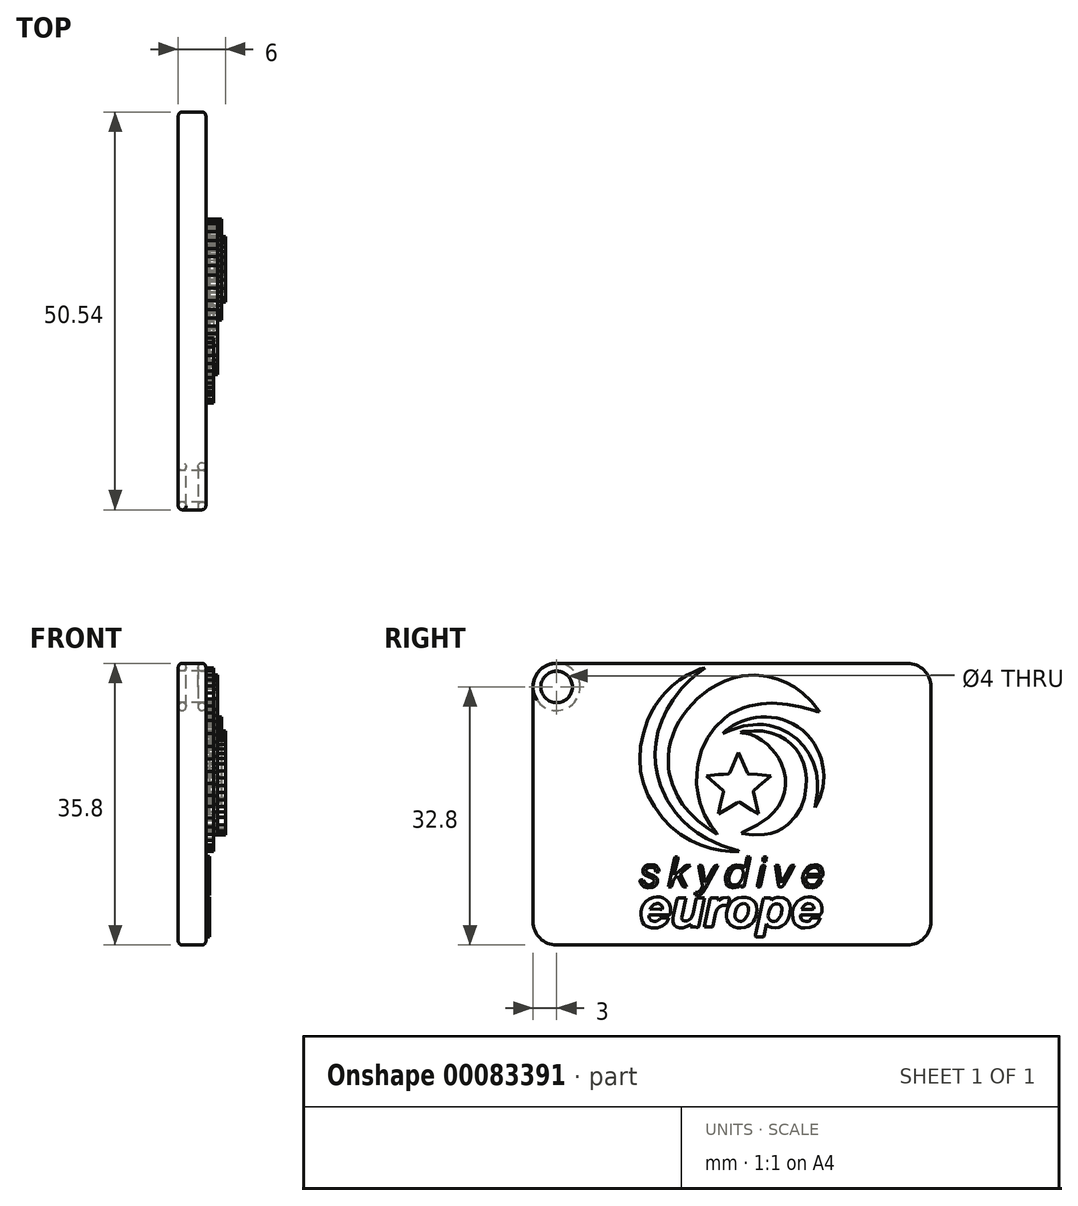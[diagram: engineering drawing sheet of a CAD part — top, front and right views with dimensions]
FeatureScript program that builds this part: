
annotation { "Feature Type Name" : "Feature", "Feature Type Description" : "" }
export const myFeature = defineFeature(function(context is Context, id is Id, definition is map)
    precondition{}
    {
        {
            var Q0;
            Q0=qCreatedBy(makeId("Right.planeOp"),FACE);
            var sketch = newSketch(context, id + "F0", { "sketchPlane" : qUnion([Q0])});
            skCircle(sketch, "E0", {"center": v(-22.27, 14.9) * mm, "radius": 2 * mm});
            skLineSegment(sketch, "E1", {"start": v(-25.27, 17.9) * mm, "end": v(-25.27, -17.9) * mm});
            skLineSegment(sketch, "E2", {"start": v(25.27, -17.9) * mm, "end": v(-25.27, -17.9) * mm});
            skLineSegment(sketch, "E3", {"start": v(25.27, 17.9) * mm, "end": v(-25.27, 17.9) * mm});
            skLineSegment(sketch, "E4", {"start": v(25.27, -17.9) * mm, "end": v(25.27, 17.9) * mm});
            skSolve(sketch);
        }
        {
            var Q0;
            Q0 = qSketchRegion(id + "F0", true);
            extrude(context, id + "F1", {"entities" : qUnion([Q0]), "depth" : 3.5 * mm});
        }
        {
            var Q0;
            Q0=makeQuery(id+"F1.opExtrude","SWEPT_EDGE",EDGE,{"disambiguationData":[OSD([sQuery(id+"F0.wireOp",EDGE,"E1"),sQuery(id+"F0.wireOp",EDGE,"E3")])]});
            var Q1;
            Q1=makeQuery(id+"F1.opExtrude","SWEPT_EDGE",EDGE,{"disambiguationData":[OSD([sQuery(id+"F0.wireOp",EDGE,"E1"),sQuery(id+"F0.wireOp",EDGE,"E2")])]});
            var Q2;
            Q2=makeQuery(id+"F1.opExtrude","SWEPT_EDGE",EDGE,{"disambiguationData":[OSD([sQuery(id+"F0.wireOp",EDGE,"E3"),sQuery(id+"F0.wireOp",EDGE,"E4")])]});
            var Q3;
            Q3=makeQuery(id+"F1.opExtrude","SWEPT_EDGE",EDGE,{"disambiguationData":[OSD([sQuery(id+"F0.wireOp",EDGE,"E2"),sQuery(id+"F0.wireOp",EDGE,"E4")])]});
            fillet(context, id + "F2", {"entities" : qUnion([Q0, Q1, Q2, Q3]), "radius" : 3 * mm, "tangentPropagation" : true, "allowEdgeOverflow" : false});
        }
        {
            var Q0;
            Q0=makeQuery(id+"F1.opExtrude","CAP_FACE",FACE,{"disambiguationData":[OSD([sQuery(id+"F0.wireOp",EDGE,"E0"),sQuery(id+"F0.wireOp",EDGE,"E1"),sQuery(id+"F0.wireOp",EDGE,"E2"),sQuery(id+"F0.wireOp",EDGE,"E3"),sQuery(id+"F0.wireOp",EDGE,"E4")])],"isStart":false});
            var Q1;
            Q1=makeQuery(id+"F1.opExtrude","CAP_FACE",FACE,{"disambiguationData":[OSD([sQuery(id+"F0.wireOp",EDGE,"E0"),sQuery(id+"F0.wireOp",EDGE,"E1"),sQuery(id+"F0.wireOp",EDGE,"E2"),sQuery(id+"F0.wireOp",EDGE,"E3"),sQuery(id+"F0.wireOp",EDGE,"E4")])],"isStart":true});
            fillet(context, id + "F3", {"entities" : qUnion([Q0, Q1]), "radius" : 0.5 * mm, "tangentPropagation" : true, "allowEdgeOverflow" : false});
        }
        {
            var Q0;
            Q0=makeQuery(id+"F1.opExtrude","CAP_EDGE",EDGE,{"disambiguationData":[OSD([sQuery(id+"F0.wireOp",EDGE,"E0")])],"isStart":false});
            var Q1;
            Q1=makeQuery(id+"F1.opExtrude","CAP_EDGE",EDGE,{"disambiguationData":[OSD([sQuery(id+"F0.wireOp",EDGE,"E0")])],"isStart":true});
            fillet(context, id + "F4", {"entities" : qUnion([Q0, Q1]), "radius" : 0.3 * mm, "tangentPropagation" : true, "allowEdgeOverflow" : false});
        }
        {
            var Q0;
            Q0=makeQuery(id+"F1.opExtrude","CAP_FACE",FACE,{"disambiguationData":[OSD([sQuery(id+"F0.wireOp",EDGE,"E0"),sQuery(id+"F0.wireOp",EDGE,"E1"),sQuery(id+"F0.wireOp",EDGE,"E2"),sQuery(id+"F0.wireOp",EDGE,"E3"),sQuery(id+"F0.wireOp",EDGE,"E4")])],"isStart":false});
            var sketch = newSketch(context, id + "F5", { "sketchPlane" : qUnion([Q0])});
            skLineSegment(sketch, "E5", {"start": v(4.97, 3.61) * mm, "end": v(3.46, 2.32) * mm});
            skLineSegment(sketch, "E6", {"start": v(3.46, 2.32) * mm, "end": v(3.2, 2.08) * mm});
            skLineSegment(sketch, "E7", {"start": v(3.2, 2.08) * mm, "end": v(2.92, 1.86) * mm});
            skLineSegment(sketch, "E8", {"start": v(2.92, 1.86) * mm, "end": v(2.8, 1.76) * mm});
            skLineSegment(sketch, "E9", {"start": v(2.8, 1.76) * mm, "end": v(2.75, 1.64) * mm});
            skLineSegment(sketch, "E10", {"start": v(2.75, 1.64) * mm, "end": v(2.74, 1.5) * mm});
            skLineSegment(sketch, "E11", {"start": v(2.74, 1.5) * mm, "end": v(2.78, 1.33) * mm});
            skLineSegment(sketch, "E12", {"start": v(2.78, 1.33) * mm, "end": v(3.38, -1.24) * mm});
            skLineSegment(sketch, "E13", {"start": v(3.38, -1.24) * mm, "end": v(2.49, -0.72) * mm});
            skLineSegment(sketch, "E14", {"start": v(2.49, -0.72) * mm, "end": v(1.01, 0.2) * mm});
            skLineSegment(sketch, "E15", {"start": v(1.01, 0.2) * mm, "end": v(0.83, 0.26) * mm});
            skLineSegment(sketch, "E16", {"start": v(0.83, 0.26) * mm, "end": v(0.62, 0.18) * mm});
            skLineSegment(sketch, "E17", {"start": v(0.62, 0.18) * mm, "end": v(-0.53, -0.53) * mm});
            skLineSegment(sketch, "E18", {"start": v(-0.53, -0.53) * mm, "end": v(-1.73, -1.25) * mm});
            skLineSegment(sketch, "E19", {"start": v(-1.73, -1.25) * mm, "end": v(-1.44, 0.02) * mm});
            skLineSegment(sketch, "E20", {"start": v(-1.44, 0.02) * mm, "end": v(-1.26, 0.8) * mm});
            skLineSegment(sketch, "E21", {"start": v(-1.26, 0.8) * mm, "end": v(-1.06, 1.56) * mm});
            skLineSegment(sketch, "E22", {"start": v(-1.06, 1.56) * mm, "end": v(-1.07, 1.68) * mm});
            skLineSegment(sketch, "E23", {"start": v(-1.07, 1.68) * mm, "end": v(-1.17, 1.77) * mm});
            skLineSegment(sketch, "E24", {"start": v(-1.17, 1.77) * mm, "end": v(-3.2, 3.53) * mm});
            skLineSegment(sketch, "E25", {"start": v(-3.2, 3.53) * mm, "end": v(-3.22, 3.56) * mm});
            skLineSegment(sketch, "E26", {"start": v(-3.22, 3.56) * mm, "end": v(-3.27, 3.61) * mm});
            skLineSegment(sketch, "E27", {"start": v(-3.27, 3.61) * mm, "end": v(-1.68, 3.76) * mm});
            skLineSegment(sketch, "E28", {"start": v(-1.68, 3.76) * mm, "end": v(-1.07, 3.8) * mm});
            skLineSegment(sketch, "E29", {"start": v(-1.07, 3.8) * mm, "end": v(-0.45, 3.86) * mm});
            skLineSegment(sketch, "E30", {"start": v(-0.45, 3.86) * mm, "end": v(-0.37, 3.89) * mm});
            skLineSegment(sketch, "E31", {"start": v(-0.37, 3.89) * mm, "end": v(-0.32, 3.94) * mm});
            skLineSegment(sketch, "E32", {"start": v(-0.32, 3.94) * mm, "end": v(-0.3, 4) * mm});
            skLineSegment(sketch, "E33", {"start": v(-0.3, 4) * mm, "end": v(-0.27, 4.05) * mm});
            skLineSegment(sketch, "E34", {"start": v(-0.27, 4.05) * mm, "end": v(0.8, 6.6) * mm});
            skLineSegment(sketch, "E35", {"start": v(0.8, 6.6) * mm, "end": v(1.1, 6.02) * mm});
            skLineSegment(sketch, "E36", {"start": v(1.1, 6.02) * mm, "end": v(1.34, 5.44) * mm});
            skLineSegment(sketch, "E37", {"start": v(1.34, 5.44) * mm, "end": v(1.94, 3.97) * mm});
            skLineSegment(sketch, "E38", {"start": v(1.94, 3.97) * mm, "end": v(2, 3.89) * mm});
            skLineSegment(sketch, "E39", {"start": v(2, 3.89) * mm, "end": v(2.08, 3.86) * mm});
            skLineSegment(sketch, "E40", {"start": v(2.08, 3.86) * mm, "end": v(3.22, 3.76) * mm});
            skLineSegment(sketch, "E41", {"start": v(3.22, 3.76) * mm, "end": v(4.97, 3.61) * mm});
            skLineSegment(sketch, "E42", {"start": v(4.37, -15.22) * mm, "end": v(4.05, -16.78) * mm});
            skLineSegment(sketch, "E43", {"start": v(4.05, -16.78) * mm, "end": v(4, -16.87) * mm});
            skLineSegment(sketch, "E44", {"start": v(4, -16.87) * mm, "end": v(3.9, -16.88) * mm});
            skLineSegment(sketch, "E45", {"start": v(3.9, -16.88) * mm, "end": v(3.46, -16.88) * mm});
            skLineSegment(sketch, "E46", {"start": v(3.46, -16.88) * mm, "end": v(3.28, -16.88) * mm});
            skLineSegment(sketch, "E47", {"start": v(3.28, -16.88) * mm, "end": v(3.14, -16.87) * mm});
            skLineSegment(sketch, "E48", {"start": v(3.14, -16.87) * mm, "end": v(3.05, -16.85) * mm});
            skLineSegment(sketch, "E49", {"start": v(3.05, -16.85) * mm, "end": v(3, -16.81) * mm});
            skLineSegment(sketch, "E50", {"start": v(3, -16.81) * mm, "end": v(2.98, -16.75) * mm});
            skLineSegment(sketch, "E51", {"start": v(2.98, -16.75) * mm, "end": v(2.98, -16.65) * mm});
            skLineSegment(sketch, "E52", {"start": v(2.98, -16.65) * mm, "end": v(3, -16.52) * mm});
            skLineSegment(sketch, "E53", {"start": v(3, -16.52) * mm, "end": v(3.05, -16.34) * mm});
            skLineSegment(sketch, "E54", {"start": v(3.05, -16.34) * mm, "end": v(3.75, -13.08) * mm});
            skLineSegment(sketch, "E55", {"start": v(3.75, -13.08) * mm, "end": v(3.94, -12.17) * mm});
            skLineSegment(sketch, "E56", {"start": v(3.94, -12.17) * mm, "end": v(3.98, -12.03) * mm});
            skLineSegment(sketch, "E57", {"start": v(3.98, -12.03) * mm, "end": v(4.04, -11.94) * mm});
            skLineSegment(sketch, "E58", {"start": v(4.04, -11.94) * mm, "end": v(4.15, -11.89) * mm});
            skLineSegment(sketch, "E59", {"start": v(4.15, -11.89) * mm, "end": v(4.3, -11.9) * mm});
            skLineSegment(sketch, "E60", {"start": v(4.3, -11.9) * mm, "end": v(4.5, -11.91) * mm});
            skLineSegment(sketch, "E61", {"start": v(4.5, -11.91) * mm, "end": v(4.72, -11.9) * mm});
            skLineSegment(sketch, "E62", {"start": v(4.72, -11.9) * mm, "end": v(4.86, -11.9) * mm});
            skLineSegment(sketch, "E63", {"start": v(4.86, -11.9) * mm, "end": v(4.96, -11.94) * mm});
            skLineSegment(sketch, "E64", {"start": v(4.96, -11.94) * mm, "end": v(5, -12.06) * mm});
            skLineSegment(sketch, "E65", {"start": v(5, -12.06) * mm, "end": v(4.99, -12.25) * mm});
            skLineSegment(sketch, "E66", {"start": v(4.99, -12.25) * mm, "end": v(5.22, -12.03) * mm});
            skLineSegment(sketch, "E67", {"start": v(5.22, -12.03) * mm, "end": v(5.47, -11.9) * mm});
            skLineSegment(sketch, "E68", {"start": v(5.47, -11.9) * mm, "end": v(5.73, -11.85) * mm});
            skLineSegment(sketch, "E69", {"start": v(5.73, -11.85) * mm, "end": v(6, -11.83) * mm});
            skLineSegment(sketch, "E70", {"start": v(6, -11.83) * mm, "end": v(6.52, -11.9) * mm});
            skLineSegment(sketch, "E71", {"start": v(6.52, -11.9) * mm, "end": v(6.98, -12.14) * mm});
            skLineSegment(sketch, "E72", {"start": v(6.98, -12.14) * mm, "end": v(7.13, -12.3) * mm});
            skLineSegment(sketch, "E73", {"start": v(7.13, -12.3) * mm, "end": v(7.24, -12.46) * mm});
            skLineSegment(sketch, "E74", {"start": v(7.24, -12.46) * mm, "end": v(7.32, -12.65) * mm});
            skLineSegment(sketch, "E75", {"start": v(7.32, -12.65) * mm, "end": v(7.37, -12.86) * mm});
            skLineSegment(sketch, "E76", {"start": v(7.37, -12.86) * mm, "end": v(7.41, -13.26) * mm});
            skLineSegment(sketch, "E77", {"start": v(7.41, -13.26) * mm, "end": v(7.4, -13.68) * mm});
            skLineSegment(sketch, "E78", {"start": v(7.4, -13.68) * mm, "end": v(7.31, -14.1) * mm});
            skLineSegment(sketch, "E79", {"start": v(7.31, -14.1) * mm, "end": v(7.18, -14.51) * mm});
            skLineSegment(sketch, "E80", {"start": v(7.18, -14.51) * mm, "end": v(6.98, -14.89) * mm});
            skLineSegment(sketch, "E81", {"start": v(6.98, -14.89) * mm, "end": v(6.71, -15.21) * mm});
            skLineSegment(sketch, "E82", {"start": v(6.71, -15.21) * mm, "end": v(6.38, -15.47) * mm});
            skLineSegment(sketch, "E83", {"start": v(6.38, -15.47) * mm, "end": v(5.98, -15.64) * mm});
            skLineSegment(sketch, "E84", {"start": v(5.98, -15.64) * mm, "end": v(5.5, -15.71) * mm});
            skLineSegment(sketch, "E85", {"start": v(5.5, -15.71) * mm, "end": v(5.05, -15.67) * mm});
            skLineSegment(sketch, "E86", {"start": v(5.05, -15.67) * mm, "end": v(4.66, -15.5) * mm});
            skLineSegment(sketch, "E87", {"start": v(4.66, -15.5) * mm, "end": v(4.37, -15.22) * mm});
            skLineSegment(sketch, "E88", {"start": v(-8, -14.42) * mm, "end": v(-8.34, -15.06) * mm});
            skLineSegment(sketch, "E89", {"start": v(-8.34, -15.06) * mm, "end": v(-8.85, -15.49) * mm});
            skLineSegment(sketch, "E90", {"start": v(-8.85, -15.49) * mm, "end": v(-9.49, -15.7) * mm});
            skLineSegment(sketch, "E91", {"start": v(-9.49, -15.7) * mm, "end": v(-10.23, -15.7) * mm});
            skLineSegment(sketch, "E92", {"start": v(-10.23, -15.7) * mm, "end": v(-10.6, -15.61) * mm});
            skLineSegment(sketch, "E93", {"start": v(-10.6, -15.61) * mm, "end": v(-10.93, -15.47) * mm});
            skLineSegment(sketch, "E94", {"start": v(-10.93, -15.47) * mm, "end": v(-11.19, -15.25) * mm});
            skLineSegment(sketch, "E95", {"start": v(-11.19, -15.25) * mm, "end": v(-11.37, -14.96) * mm});
            skLineSegment(sketch, "E96", {"start": v(-11.37, -14.96) * mm, "end": v(-11.5, -14.52) * mm});
            skLineSegment(sketch, "E97", {"start": v(-11.5, -14.52) * mm, "end": v(-11.56, -14.06) * mm});
            skLineSegment(sketch, "E98", {"start": v(-11.56, -14.06) * mm, "end": v(-11.54, -13.6) * mm});
            skLineSegment(sketch, "E99", {"start": v(-11.54, -13.6) * mm, "end": v(-11.42, -13.14) * mm});
            skLineSegment(sketch, "E100", {"start": v(-11.42, -13.14) * mm, "end": v(-11.2, -12.72) * mm});
            skLineSegment(sketch, "E101", {"start": v(-11.2, -12.72) * mm, "end": v(-10.9, -12.36) * mm});
            skLineSegment(sketch, "E102", {"start": v(-10.9, -12.36) * mm, "end": v(-10.5, -12.06) * mm});
            skLineSegment(sketch, "E103", {"start": v(-10.5, -12.06) * mm, "end": v(-9.99, -11.87) * mm});
            skLineSegment(sketch, "E104", {"start": v(-9.99, -11.87) * mm, "end": v(-9.58, -11.8) * mm});
            skLineSegment(sketch, "E105", {"start": v(-9.58, -11.8) * mm, "end": v(-9.16, -11.81) * mm});
            skLineSegment(sketch, "E106", {"start": v(-9.16, -11.81) * mm, "end": v(-8.75, -11.92) * mm});
            skLineSegment(sketch, "E107", {"start": v(-8.75, -11.92) * mm, "end": v(-8.36, -12.14) * mm});
            skLineSegment(sketch, "E108", {"start": v(-8.36, -12.14) * mm, "end": v(-7.99, -12.57) * mm});
            skLineSegment(sketch, "E109", {"start": v(-7.99, -12.57) * mm, "end": v(-7.83, -13.1) * mm});
            skLineSegment(sketch, "E110", {"start": v(-7.83, -13.1) * mm, "end": v(-7.82, -13.45) * mm});
            skLineSegment(sketch, "E111", {"start": v(-7.82, -13.45) * mm, "end": v(-7.82, -13.8) * mm});
            skLineSegment(sketch, "E112", {"start": v(-7.82, -13.8) * mm, "end": v(-7.83, -13.93) * mm});
            skLineSegment(sketch, "E113", {"start": v(-7.83, -13.93) * mm, "end": v(-7.88, -14.01) * mm});
            skLineSegment(sketch, "E114", {"start": v(-7.88, -14.01) * mm, "end": v(-7.97, -14.05) * mm});
            skLineSegment(sketch, "E115", {"start": v(-7.97, -14.05) * mm, "end": v(-8.1, -14.06) * mm});
            skLineSegment(sketch, "E116", {"start": v(-8.1, -14.06) * mm, "end": v(-10.23, -14.06) * mm});
            skLineSegment(sketch, "E117", {"start": v(-10.23, -14.06) * mm, "end": v(-10.42, -14.08) * mm});
            skLineSegment(sketch, "E118", {"start": v(-10.42, -14.08) * mm, "end": v(-10.52, -14.16) * mm});
            skLineSegment(sketch, "E119", {"start": v(-10.52, -14.16) * mm, "end": v(-10.54, -14.3) * mm});
            skLineSegment(sketch, "E120", {"start": v(-10.54, -14.3) * mm, "end": v(-10.48, -14.5) * mm});
            skLineSegment(sketch, "E121", {"start": v(-10.48, -14.5) * mm, "end": v(-10.26, -14.77) * mm});
            skLineSegment(sketch, "E122", {"start": v(-10.26, -14.77) * mm, "end": v(-9.93, -14.9) * mm});
            skLineSegment(sketch, "E123", {"start": v(-9.93, -14.9) * mm, "end": v(-9.57, -14.87) * mm});
            skLineSegment(sketch, "E124", {"start": v(-9.57, -14.87) * mm, "end": v(-9.23, -14.63) * mm});
            skLineSegment(sketch, "E125", {"start": v(-9.23, -14.63) * mm, "end": v(-9.13, -14.53) * mm});
            skLineSegment(sketch, "E126", {"start": v(-9.13, -14.53) * mm, "end": v(-9.02, -14.46) * mm});
            skLineSegment(sketch, "E127", {"start": v(-9.02, -14.46) * mm, "end": v(-8.9, -14.42) * mm});
            skLineSegment(sketch, "E128", {"start": v(-8.9, -14.42) * mm, "end": v(-8.77, -14.42) * mm});
            skLineSegment(sketch, "E129", {"start": v(-8.77, -14.42) * mm, "end": v(-8, -14.42) * mm});
            skLineSegment(sketch, "E130", {"start": v(11.25, -14.42) * mm, "end": v(10.9, -15.08) * mm});
            skLineSegment(sketch, "E131", {"start": v(10.9, -15.08) * mm, "end": v(10.45, -15.48) * mm});
            skLineSegment(sketch, "E132", {"start": v(10.45, -15.48) * mm, "end": v(9.92, -15.67) * mm});
            skLineSegment(sketch, "E133", {"start": v(9.92, -15.67) * mm, "end": v(9.3, -15.73) * mm});
            skLineSegment(sketch, "E134", {"start": v(9.3, -15.73) * mm, "end": v(8.84, -15.7) * mm});
            skLineSegment(sketch, "E135", {"start": v(8.84, -15.7) * mm, "end": v(8.42, -15.55) * mm});
            skLineSegment(sketch, "E136", {"start": v(8.42, -15.55) * mm, "end": v(8.07, -15.3) * mm});
            skLineSegment(sketch, "E137", {"start": v(8.07, -15.3) * mm, "end": v(7.84, -14.9) * mm});
            skLineSegment(sketch, "E138", {"start": v(7.84, -14.9) * mm, "end": v(7.72, -14.47) * mm});
            skLineSegment(sketch, "E139", {"start": v(7.72, -14.47) * mm, "end": v(7.68, -14.02) * mm});
            skLineSegment(sketch, "E140", {"start": v(7.68, -14.02) * mm, "end": v(7.71, -13.57) * mm});
            skLineSegment(sketch, "E141", {"start": v(7.71, -13.57) * mm, "end": v(7.83, -13.13) * mm});
            skLineSegment(sketch, "E142", {"start": v(7.83, -13.13) * mm, "end": v(8.03, -12.72) * mm});
            skLineSegment(sketch, "E143", {"start": v(8.03, -12.72) * mm, "end": v(8.33, -12.36) * mm});
            skLineSegment(sketch, "E144", {"start": v(8.33, -12.36) * mm, "end": v(8.73, -12.07) * mm});
            skLineSegment(sketch, "E145", {"start": v(8.73, -12.07) * mm, "end": v(9.23, -11.87) * mm});
            skLineSegment(sketch, "E146", {"start": v(9.23, -11.87) * mm, "end": v(9.66, -11.8) * mm});
            skLineSegment(sketch, "E147", {"start": v(9.66, -11.8) * mm, "end": v(10.1, -11.81) * mm});
            skLineSegment(sketch, "E148", {"start": v(10.1, -11.81) * mm, "end": v(10.52, -11.93) * mm});
            skLineSegment(sketch, "E149", {"start": v(10.52, -11.93) * mm, "end": v(10.92, -12.16) * mm});
            skLineSegment(sketch, "E150", {"start": v(10.92, -12.16) * mm, "end": v(11.12, -12.35) * mm});
            skLineSegment(sketch, "E151", {"start": v(11.12, -12.35) * mm, "end": v(11.27, -12.58) * mm});
            skLineSegment(sketch, "E152", {"start": v(11.27, -12.58) * mm, "end": v(11.37, -12.83) * mm});
            skLineSegment(sketch, "E153", {"start": v(11.37, -12.83) * mm, "end": v(11.42, -13.11) * mm});
            skLineSegment(sketch, "E154", {"start": v(11.42, -13.11) * mm, "end": v(11.43, -13.43) * mm});
            skLineSegment(sketch, "E155", {"start": v(11.43, -13.43) * mm, "end": v(11.42, -13.66) * mm});
            skLineSegment(sketch, "E156", {"start": v(11.42, -13.66) * mm, "end": v(11.4, -13.83) * mm});
            skLineSegment(sketch, "E157", {"start": v(11.4, -13.83) * mm, "end": v(11.33, -13.94) * mm});
            skLineSegment(sketch, "E158", {"start": v(11.33, -13.94) * mm, "end": v(11.22, -14) * mm});
            skLineSegment(sketch, "E159", {"start": v(11.22, -14) * mm, "end": v(11.05, -14.04) * mm});
            skLineSegment(sketch, "E160", {"start": v(11.05, -14.04) * mm, "end": v(10.82, -14.06) * mm});
            skLineSegment(sketch, "E161", {"start": v(10.82, -14.06) * mm, "end": v(10.5, -14.06) * mm});
            skLineSegment(sketch, "E162", {"start": v(10.5, -14.06) * mm, "end": v(8.92, -14.06) * mm});
            skLineSegment(sketch, "E163", {"start": v(8.92, -14.06) * mm, "end": v(8.82, -14.06) * mm});
            skLineSegment(sketch, "E164", {"start": v(8.82, -14.06) * mm, "end": v(8.76, -14.1) * mm});
            skLineSegment(sketch, "E165", {"start": v(8.76, -14.1) * mm, "end": v(8.73, -14.15) * mm});
            skLineSegment(sketch, "E166", {"start": v(8.73, -14.15) * mm, "end": v(8.72, -14.25) * mm});
            skLineSegment(sketch, "E167", {"start": v(8.72, -14.25) * mm, "end": v(8.75, -14.45) * mm});
            skLineSegment(sketch, "E168", {"start": v(8.75, -14.45) * mm, "end": v(8.82, -14.61) * mm});
            skLineSegment(sketch, "E169", {"start": v(8.82, -14.61) * mm, "end": v(8.95, -14.74) * mm});
            skLineSegment(sketch, "E170", {"start": v(8.95, -14.74) * mm, "end": v(9.12, -14.84) * mm});
            skLineSegment(sketch, "E171", {"start": v(9.12, -14.84) * mm, "end": v(9.38, -14.9) * mm});
            skLineSegment(sketch, "E172", {"start": v(9.38, -14.9) * mm, "end": v(9.63, -14.9) * mm});
            skLineSegment(sketch, "E173", {"start": v(9.63, -14.9) * mm, "end": v(9.85, -14.8) * mm});
            skLineSegment(sketch, "E174", {"start": v(9.85, -14.8) * mm, "end": v(10, -14.66) * mm});
            skLineSegment(sketch, "E175", {"start": v(10, -14.66) * mm, "end": v(10.1, -14.52) * mm});
            skLineSegment(sketch, "E176", {"start": v(10.1, -14.52) * mm, "end": v(10.22, -14.45) * mm});
            skLineSegment(sketch, "E177", {"start": v(10.22, -14.45) * mm, "end": v(10.36, -14.42) * mm});
            skLineSegment(sketch, "E178", {"start": v(10.36, -14.42) * mm, "end": v(10.5, -14.42) * mm});
            skLineSegment(sketch, "E179", {"start": v(10.5, -14.42) * mm, "end": v(11.25, -14.42) * mm});
            skLineSegment(sketch, "E180", {"start": v(3.15, -13.4) * mm, "end": v(3.14, -13.83) * mm});
            skLineSegment(sketch, "E181", {"start": v(3.14, -13.83) * mm, "end": v(3.06, -14.21) * mm});
            skLineSegment(sketch, "E182", {"start": v(3.06, -14.21) * mm, "end": v(2.93, -14.56) * mm});
            skLineSegment(sketch, "E183", {"start": v(2.93, -14.56) * mm, "end": v(2.75, -14.87) * mm});
            skLineSegment(sketch, "E184", {"start": v(2.75, -14.87) * mm, "end": v(2.52, -15.14) * mm});
            skLineSegment(sketch, "E185", {"start": v(2.52, -15.14) * mm, "end": v(2.26, -15.36) * mm});
            skLineSegment(sketch, "E186", {"start": v(2.26, -15.36) * mm, "end": v(1.97, -15.52) * mm});
            skLineSegment(sketch, "E187", {"start": v(1.97, -15.52) * mm, "end": v(1.65, -15.64) * mm});
            skLineSegment(sketch, "E188", {"start": v(1.65, -15.64) * mm, "end": v(1.16, -15.73) * mm});
            skLineSegment(sketch, "E189", {"start": v(1.16, -15.73) * mm, "end": v(0.69, -15.72) * mm});
            skLineSegment(sketch, "E190", {"start": v(0.69, -15.72) * mm, "end": v(0.23, -15.6) * mm});
            skLineSegment(sketch, "E191", {"start": v(0.23, -15.6) * mm, "end": v(-0.2, -15.34) * mm});
            skLineSegment(sketch, "E192", {"start": v(-0.2, -15.34) * mm, "end": v(-0.47, -15.04) * mm});
            skLineSegment(sketch, "E193", {"start": v(-0.47, -15.04) * mm, "end": v(-0.63, -14.7) * mm});
            skLineSegment(sketch, "E194", {"start": v(-0.63, -14.7) * mm, "end": v(-0.69, -14.3) * mm});
            skLineSegment(sketch, "E195", {"start": v(-0.69, -14.3) * mm, "end": v(-0.68, -13.9) * mm});
            skLineSegment(sketch, "E196", {"start": v(-0.68, -13.9) * mm, "end": v(-0.57, -13.3) * mm});
            skLineSegment(sketch, "E197", {"start": v(-0.57, -13.3) * mm, "end": v(-0.3, -12.74) * mm});
            skLineSegment(sketch, "E198", {"start": v(-0.3, -12.74) * mm, "end": v(0, -12.38) * mm});
            skLineSegment(sketch, "E199", {"start": v(0, -12.38) * mm, "end": v(0.35, -12.1) * mm});
            skLineSegment(sketch, "E200", {"start": v(0.35, -12.1) * mm, "end": v(0.75, -11.91) * mm});
            skLineSegment(sketch, "E201", {"start": v(0.75, -11.91) * mm, "end": v(1.22, -11.84) * mm});
            skLineSegment(sketch, "E202", {"start": v(1.22, -11.84) * mm, "end": v(1.75, -11.84) * mm});
            skLineSegment(sketch, "E203", {"start": v(1.75, -11.84) * mm, "end": v(2.27, -11.95) * mm});
            skLineSegment(sketch, "E204", {"start": v(2.27, -11.95) * mm, "end": v(2.7, -12.2) * mm});
            skLineSegment(sketch, "E205", {"start": v(2.7, -12.2) * mm, "end": v(2.98, -12.53) * mm});
            skLineSegment(sketch, "E206", {"start": v(2.98, -12.53) * mm, "end": v(3.13, -12.93) * mm});
            skLineSegment(sketch, "E207", {"start": v(3.13, -12.93) * mm, "end": v(3.15, -13.4) * mm});
            skLineSegment(sketch, "E208", {"start": v(-3.46, -11.9) * mm, "end": v(-4.05, -14.79) * mm});
            skLineSegment(sketch, "E209", {"start": v(-4.05, -14.79) * mm, "end": v(-4.18, -15.41) * mm});
            skLineSegment(sketch, "E210", {"start": v(-4.18, -15.41) * mm, "end": v(-4.21, -15.5) * mm});
            skLineSegment(sketch, "E211", {"start": v(-4.21, -15.5) * mm, "end": v(-4.26, -15.58) * mm});
            skLineSegment(sketch, "E212", {"start": v(-4.26, -15.58) * mm, "end": v(-4.34, -15.62) * mm});
            skLineSegment(sketch, "E213", {"start": v(-4.34, -15.62) * mm, "end": v(-4.46, -15.62) * mm});
            skLineSegment(sketch, "E214", {"start": v(-4.46, -15.62) * mm, "end": v(-4.7, -15.61) * mm});
            skLineSegment(sketch, "E215", {"start": v(-4.7, -15.61) * mm, "end": v(-4.97, -15.62) * mm});
            skLineSegment(sketch, "E216", {"start": v(-4.97, -15.62) * mm, "end": v(-5.07, -15.62) * mm});
            skLineSegment(sketch, "E217", {"start": v(-5.07, -15.62) * mm, "end": v(-5.15, -15.61) * mm});
            skLineSegment(sketch, "E218", {"start": v(-5.15, -15.61) * mm, "end": v(-5.2, -15.6) * mm});
            skLineSegment(sketch, "E219", {"start": v(-5.2, -15.6) * mm, "end": v(-5.24, -15.57) * mm});
            skLineSegment(sketch, "E220", {"start": v(-5.24, -15.57) * mm, "end": v(-5.25, -15.53) * mm});
            skLineSegment(sketch, "E221", {"start": v(-5.25, -15.53) * mm, "end": v(-5.24, -15.46) * mm});
            skLineSegment(sketch, "E222", {"start": v(-5.24, -15.46) * mm, "end": v(-5.22, -15.37) * mm});
            skLineSegment(sketch, "E223", {"start": v(-5.22, -15.37) * mm, "end": v(-5.18, -15.25) * mm});
            skLineSegment(sketch, "E224", {"start": v(-5.18, -15.25) * mm, "end": v(-5.69, -15.56) * mm});
            skLineSegment(sketch, "E225", {"start": v(-5.69, -15.56) * mm, "end": v(-6.23, -15.73) * mm});
            skLineSegment(sketch, "E226", {"start": v(-6.23, -15.73) * mm, "end": v(-6.65, -15.73) * mm});
            skLineSegment(sketch, "E227", {"start": v(-6.65, -15.73) * mm, "end": v(-7.05, -15.58) * mm});
            skLineSegment(sketch, "E228", {"start": v(-7.05, -15.58) * mm, "end": v(-7.34, -15.32) * mm});
            skLineSegment(sketch, "E229", {"start": v(-7.34, -15.32) * mm, "end": v(-7.46, -14.98) * mm});
            skLineSegment(sketch, "E230", {"start": v(-7.46, -14.98) * mm, "end": v(-7.46, -14.51) * mm});
            skLineSegment(sketch, "E231", {"start": v(-7.46, -14.51) * mm, "end": v(-7.4, -14.04) * mm});
            skLineSegment(sketch, "E232", {"start": v(-7.4, -14.04) * mm, "end": v(-6.98, -12.12) * mm});
            skLineSegment(sketch, "E233", {"start": v(-6.98, -12.12) * mm, "end": v(-6.96, -12.02) * mm});
            skLineSegment(sketch, "E234", {"start": v(-6.96, -12.02) * mm, "end": v(-6.92, -11.95) * mm});
            skLineSegment(sketch, "E235", {"start": v(-6.92, -11.95) * mm, "end": v(-6.85, -11.9) * mm});
            skLineSegment(sketch, "E236", {"start": v(-6.85, -11.9) * mm, "end": v(-6.74, -11.9) * mm});
            skLineSegment(sketch, "E237", {"start": v(-6.74, -11.9) * mm, "end": v(-6.3, -11.9) * mm});
            skLineSegment(sketch, "E238", {"start": v(-6.3, -11.9) * mm, "end": v(-5.85, -11.9) * mm});
            skLineSegment(sketch, "E239", {"start": v(-5.85, -11.9) * mm, "end": v(-6.38, -14.35) * mm});
            skLineSegment(sketch, "E240", {"start": v(-6.38, -14.35) * mm, "end": v(-6.4, -14.48) * mm});
            skLineSegment(sketch, "E241", {"start": v(-6.4, -14.48) * mm, "end": v(-6.37, -14.6) * mm});
            skLineSegment(sketch, "E242", {"start": v(-6.37, -14.6) * mm, "end": v(-6.31, -14.7) * mm});
            skLineSegment(sketch, "E243", {"start": v(-6.31, -14.7) * mm, "end": v(-6.2, -14.78) * mm});
            skLineSegment(sketch, "E244", {"start": v(-6.2, -14.78) * mm, "end": v(-6.01, -14.84) * mm});
            skLineSegment(sketch, "E245", {"start": v(-6.01, -14.84) * mm, "end": v(-5.82, -14.85) * mm});
            skLineSegment(sketch, "E246", {"start": v(-5.82, -14.85) * mm, "end": v(-5.64, -14.82) * mm});
            skLineSegment(sketch, "E247", {"start": v(-5.64, -14.82) * mm, "end": v(-5.45, -14.72) * mm});
            skLineSegment(sketch, "E248", {"start": v(-5.45, -14.72) * mm, "end": v(-5.23, -14.5) * mm});
            skLineSegment(sketch, "E249", {"start": v(-5.23, -14.5) * mm, "end": v(-5.07, -14.24) * mm});
            skLineSegment(sketch, "E250", {"start": v(-5.07, -14.24) * mm, "end": v(-4.96, -13.96) * mm});
            skLineSegment(sketch, "E251", {"start": v(-4.96, -13.96) * mm, "end": v(-4.89, -13.66) * mm});
            skLineSegment(sketch, "E252", {"start": v(-4.89, -13.66) * mm, "end": v(-4.58, -12.1) * mm});
            skLineSegment(sketch, "E253", {"start": v(-4.58, -12.1) * mm, "end": v(-4.56, -12.02) * mm});
            skLineSegment(sketch, "E254", {"start": v(-4.56, -12.02) * mm, "end": v(-4.53, -11.96) * mm});
            skLineSegment(sketch, "E255", {"start": v(-4.53, -11.96) * mm, "end": v(-4.48, -11.91) * mm});
            skLineSegment(sketch, "E256", {"start": v(-4.48, -11.91) * mm, "end": v(-4.38, -11.9) * mm});
            skLineSegment(sketch, "E257", {"start": v(-4.38, -11.9) * mm, "end": v(-3.46, -11.9) * mm});
            skLineSegment(sketch, "E258", {"start": v(-1.72, -11.9) * mm, "end": v(-1.73, -12) * mm});
            skLineSegment(sketch, "E259", {"start": v(-1.73, -12) * mm, "end": v(-1.76, -12.07) * mm});
            skLineSegment(sketch, "E260", {"start": v(-1.76, -12.07) * mm, "end": v(-1.77, -12.15) * mm});
            skLineSegment(sketch, "E261", {"start": v(-1.77, -12.15) * mm, "end": v(-1.74, -12.24) * mm});
            skLineSegment(sketch, "E262", {"start": v(-1.74, -12.24) * mm, "end": v(-1.18, -11.92) * mm});
            skLineSegment(sketch, "E263", {"start": v(-1.18, -11.92) * mm, "end": v(-0.52, -11.83) * mm});
            skLineSegment(sketch, "E264", {"start": v(-0.52, -11.83) * mm, "end": v(-0.42, -11.85) * mm});
            skLineSegment(sketch, "E265", {"start": v(-0.42, -11.85) * mm, "end": v(-0.35, -11.89) * mm});
            skLineSegment(sketch, "E266", {"start": v(-0.35, -11.89) * mm, "end": v(-0.33, -11.95) * mm});
            skLineSegment(sketch, "E267", {"start": v(-0.33, -11.95) * mm, "end": v(-0.33, -12.04) * mm});
            skLineSegment(sketch, "E268", {"start": v(-0.33, -12.04) * mm, "end": v(-0.46, -12.7) * mm});
            skLineSegment(sketch, "E269", {"start": v(-0.46, -12.7) * mm, "end": v(-0.48, -12.77) * mm});
            skLineSegment(sketch, "E270", {"start": v(-0.48, -12.77) * mm, "end": v(-0.53, -12.83) * mm});
            skLineSegment(sketch, "E271", {"start": v(-0.53, -12.83) * mm, "end": v(-0.6, -12.86) * mm});
            skLineSegment(sketch, "E272", {"start": v(-0.6, -12.86) * mm, "end": v(-0.69, -12.86) * mm});
            skLineSegment(sketch, "E273", {"start": v(-0.69, -12.86) * mm, "end": v(-1.2, -12.86) * mm});
            skLineSegment(sketch, "E274", {"start": v(-1.2, -12.86) * mm, "end": v(-1.6, -13.02) * mm});
            skLineSegment(sketch, "E275", {"start": v(-1.6, -13.02) * mm, "end": v(-1.88, -13.36) * mm});
            skLineSegment(sketch, "E276", {"start": v(-1.88, -13.36) * mm, "end": v(-2.07, -13.86) * mm});
            skLineSegment(sketch, "E277", {"start": v(-2.07, -13.86) * mm, "end": v(-2.42, -15.48) * mm});
            skLineSegment(sketch, "E278", {"start": v(-2.42, -15.48) * mm, "end": v(-2.44, -15.55) * mm});
            skLineSegment(sketch, "E279", {"start": v(-2.44, -15.55) * mm, "end": v(-2.47, -15.6) * mm});
            skLineSegment(sketch, "E280", {"start": v(-2.47, -15.6) * mm, "end": v(-2.52, -15.61) * mm});
            skLineSegment(sketch, "E281", {"start": v(-2.52, -15.61) * mm, "end": v(-2.58, -15.62) * mm});
            skLineSegment(sketch, "E282", {"start": v(-2.58, -15.62) * mm, "end": v(-3.36, -15.62) * mm});
            skLineSegment(sketch, "E283", {"start": v(-3.36, -15.62) * mm, "end": v(-3.45, -15.61) * mm});
            skLineSegment(sketch, "E284", {"start": v(-3.45, -15.61) * mm, "end": v(-3.49, -15.58) * mm});
            skLineSegment(sketch, "E285", {"start": v(-3.49, -15.58) * mm, "end": v(-3.5, -15.53) * mm});
            skLineSegment(sketch, "E286", {"start": v(-3.5, -15.53) * mm, "end": v(-3.48, -15.44) * mm});
            skLineSegment(sketch, "E287", {"start": v(-3.48, -15.44) * mm, "end": v(-2.8, -12.09) * mm});
            skLineSegment(sketch, "E288", {"start": v(-2.8, -12.09) * mm, "end": v(-2.77, -12) * mm});
            skLineSegment(sketch, "E289", {"start": v(-2.77, -12) * mm, "end": v(-2.73, -11.94) * mm});
            skLineSegment(sketch, "E290", {"start": v(-2.73, -11.94) * mm, "end": v(-2.67, -11.9) * mm});
            skLineSegment(sketch, "E291", {"start": v(-2.67, -11.9) * mm, "end": v(-2.58, -11.9) * mm});
            skLineSegment(sketch, "E292", {"start": v(-2.58, -11.9) * mm, "end": v(-1.72, -11.9) * mm});
            skLineSegment(sketch, "E293", {"start": v(1.13, -10.5) * mm, "end": v(1.12, -10.43) * mm});
            skLineSegment(sketch, "E294", {"start": v(1.12, -10.43) * mm, "end": v(1.15, -10.37) * mm});
            skLineSegment(sketch, "E295", {"start": v(1.15, -10.37) * mm, "end": v(1.18, -10.31) * mm});
            skLineSegment(sketch, "E296", {"start": v(1.18, -10.31) * mm, "end": v(1.15, -10.25) * mm});
            skLineSegment(sketch, "E297", {"start": v(1.15, -10.25) * mm, "end": v(0.87, -10.48) * mm});
            skLineSegment(sketch, "E298", {"start": v(0.87, -10.48) * mm, "end": v(0.52, -10.6) * mm});
            skLineSegment(sketch, "E299", {"start": v(0.52, -10.6) * mm, "end": v(0.14, -10.62) * mm});
            skLineSegment(sketch, "E300", {"start": v(0.14, -10.62) * mm, "end": v(-0.24, -10.53) * mm});
            skLineSegment(sketch, "E301", {"start": v(-0.24, -10.53) * mm, "end": v(-0.54, -10.31) * mm});
            skLineSegment(sketch, "E302", {"start": v(-0.54, -10.31) * mm, "end": v(-0.73, -9.98) * mm});
            skLineSegment(sketch, "E303", {"start": v(-0.73, -9.98) * mm, "end": v(-0.81, -9.6) * mm});
            skLineSegment(sketch, "E304", {"start": v(-0.81, -9.6) * mm, "end": v(-0.8, -9.25) * mm});
            skLineSegment(sketch, "E305", {"start": v(-0.8, -9.25) * mm, "end": v(-0.64, -8.68) * mm});
            skLineSegment(sketch, "E306", {"start": v(-0.64, -8.68) * mm, "end": v(-0.34, -8.17) * mm});
            skLineSegment(sketch, "E307", {"start": v(-0.34, -8.17) * mm, "end": v(0.08, -7.82) * mm});
            skLineSegment(sketch, "E308", {"start": v(0.08, -7.82) * mm, "end": v(0.58, -7.7) * mm});
            skLineSegment(sketch, "E309", {"start": v(0.58, -7.7) * mm, "end": v(1.12, -7.8) * mm});
            skLineSegment(sketch, "E310", {"start": v(1.12, -7.8) * mm, "end": v(1.62, -8.11) * mm});
            skLineSegment(sketch, "E311", {"start": v(1.62, -8.11) * mm, "end": v(1.88, -6.82) * mm});
            skLineSegment(sketch, "E312", {"start": v(1.88, -6.82) * mm, "end": v(1.93, -6.7) * mm});
            skLineSegment(sketch, "E313", {"start": v(1.93, -6.7) * mm, "end": v(2.02, -6.67) * mm});
            skLineSegment(sketch, "E314", {"start": v(2.02, -6.67) * mm, "end": v(2.11, -6.68) * mm});
            skLineSegment(sketch, "E315", {"start": v(2.11, -6.68) * mm, "end": v(2.2, -6.7) * mm});
            skLineSegment(sketch, "E316", {"start": v(2.2, -6.7) * mm, "end": v(2.28, -6.7) * mm});
            skLineSegment(sketch, "E317", {"start": v(2.28, -6.7) * mm, "end": v(2.32, -6.74) * mm});
            skLineSegment(sketch, "E318", {"start": v(2.32, -6.74) * mm, "end": v(2.32, -6.8) * mm});
            skLineSegment(sketch, "E319", {"start": v(2.32, -6.8) * mm, "end": v(2.3, -6.87) * mm});
            skLineSegment(sketch, "E320", {"start": v(2.3, -6.87) * mm, "end": v(1.59, -10.24) * mm});
            skLineSegment(sketch, "E321", {"start": v(1.59, -10.24) * mm, "end": v(1.53, -10.42) * mm});
            skLineSegment(sketch, "E322", {"start": v(1.53, -10.42) * mm, "end": v(1.43, -10.5) * mm});
            skLineSegment(sketch, "E323", {"start": v(1.43, -10.5) * mm, "end": v(1.3, -10.53) * mm});
            skLineSegment(sketch, "E324", {"start": v(1.3, -10.53) * mm, "end": v(1.13, -10.5) * mm});
            skLineSegment(sketch, "E325", {"start": v(11.4, -9.63) * mm, "end": v(11.14, -10.18) * mm});
            skLineSegment(sketch, "E326", {"start": v(11.14, -10.18) * mm, "end": v(10.74, -10.5) * mm});
            skLineSegment(sketch, "E327", {"start": v(10.74, -10.5) * mm, "end": v(10.22, -10.63) * mm});
            skLineSegment(sketch, "E328", {"start": v(10.22, -10.63) * mm, "end": v(9.65, -10.57) * mm});
            skLineSegment(sketch, "E329", {"start": v(9.65, -10.57) * mm, "end": v(9.35, -10.4) * mm});
            skLineSegment(sketch, "E330", {"start": v(9.35, -10.4) * mm, "end": v(9.13, -10.13) * mm});
            skLineSegment(sketch, "E331", {"start": v(9.13, -10.13) * mm, "end": v(9, -9.78) * mm});
            skLineSegment(sketch, "E332", {"start": v(9, -9.78) * mm, "end": v(8.97, -9.37) * mm});
            skLineSegment(sketch, "E333", {"start": v(8.97, -9.37) * mm, "end": v(9.13, -8.64) * mm});
            skLineSegment(sketch, "E334", {"start": v(9.13, -8.64) * mm, "end": v(9.56, -8.02) * mm});
            skLineSegment(sketch, "E335", {"start": v(9.56, -8.02) * mm, "end": v(9.93, -7.8) * mm});
            skLineSegment(sketch, "E336", {"start": v(9.93, -7.8) * mm, "end": v(10.4, -7.7) * mm});
            skLineSegment(sketch, "E337", {"start": v(10.4, -7.7) * mm, "end": v(10.85, -7.73) * mm});
            skLineSegment(sketch, "E338", {"start": v(10.85, -7.73) * mm, "end": v(11.21, -7.9) * mm});
            skLineSegment(sketch, "E339", {"start": v(11.21, -7.9) * mm, "end": v(11.36, -8.06) * mm});
            skLineSegment(sketch, "E340", {"start": v(11.36, -8.06) * mm, "end": v(11.46, -8.25) * mm});
            skLineSegment(sketch, "E341", {"start": v(11.46, -8.25) * mm, "end": v(11.52, -8.46) * mm});
            skLineSegment(sketch, "E342", {"start": v(11.52, -8.46) * mm, "end": v(11.54, -8.68) * mm});
            skLineSegment(sketch, "E343", {"start": v(11.54, -8.68) * mm, "end": v(11.54, -8.87) * mm});
            skLineSegment(sketch, "E344", {"start": v(11.54, -8.87) * mm, "end": v(11.53, -9.02) * mm});
            skLineSegment(sketch, "E345", {"start": v(11.53, -9.02) * mm, "end": v(11.51, -9.12) * mm});
            skLineSegment(sketch, "E346", {"start": v(11.51, -9.12) * mm, "end": v(11.47, -9.19) * mm});
            skLineSegment(sketch, "E347", {"start": v(11.47, -9.19) * mm, "end": v(11.4, -9.23) * mm});
            skLineSegment(sketch, "E348", {"start": v(11.4, -9.23) * mm, "end": v(11.3, -9.25) * mm});
            skLineSegment(sketch, "E349", {"start": v(11.3, -9.25) * mm, "end": v(11.15, -9.26) * mm});
            skLineSegment(sketch, "E350", {"start": v(11.15, -9.26) * mm, "end": v(10.96, -9.26) * mm});
            skLineSegment(sketch, "E351", {"start": v(10.96, -9.26) * mm, "end": v(9.58, -9.26) * mm});
            skLineSegment(sketch, "E352", {"start": v(9.58, -9.26) * mm, "end": v(9.49, -9.27) * mm});
            skLineSegment(sketch, "E353", {"start": v(9.49, -9.27) * mm, "end": v(9.42, -9.3) * mm});
            skLineSegment(sketch, "E354", {"start": v(9.42, -9.3) * mm, "end": v(9.39, -9.35) * mm});
            skLineSegment(sketch, "E355", {"start": v(9.39, -9.35) * mm, "end": v(9.38, -9.45) * mm});
            skLineSegment(sketch, "E356", {"start": v(9.38, -9.45) * mm, "end": v(9.42, -9.72) * mm});
            skLineSegment(sketch, "E357", {"start": v(9.42, -9.72) * mm, "end": v(9.53, -9.96) * mm});
            skLineSegment(sketch, "E358", {"start": v(9.53, -9.96) * mm, "end": v(9.7, -10.14) * mm});
            skLineSegment(sketch, "E359", {"start": v(9.7, -10.14) * mm, "end": v(9.93, -10.26) * mm});
            skLineSegment(sketch, "E360", {"start": v(9.93, -10.26) * mm, "end": v(10.19, -10.28) * mm});
            skLineSegment(sketch, "E361", {"start": v(10.19, -10.28) * mm, "end": v(10.47, -10.23) * mm});
            skLineSegment(sketch, "E362", {"start": v(10.47, -10.23) * mm, "end": v(10.7, -10.09) * mm});
            skLineSegment(sketch, "E363", {"start": v(10.7, -10.09) * mm, "end": v(10.86, -9.88) * mm});
            skLineSegment(sketch, "E364", {"start": v(10.86, -9.88) * mm, "end": v(10.96, -9.72) * mm});
            skLineSegment(sketch, "E365", {"start": v(10.96, -9.72) * mm, "end": v(11.09, -9.64) * mm});
            skLineSegment(sketch, "E366", {"start": v(11.09, -9.64) * mm, "end": v(11.24, -9.62) * mm});
            skLineSegment(sketch, "E367", {"start": v(11.24, -9.62) * mm, "end": v(11.4, -9.63) * mm});
            skLineSegment(sketch, "E368", {"start": v(-5.29, -7.8) * mm, "end": v(-6.27, -8.6) * mm});
            skLineSegment(sketch, "E369", {"start": v(-6.27, -8.6) * mm, "end": v(-6.4, -8.71) * mm});
            skLineSegment(sketch, "E370", {"start": v(-6.4, -8.71) * mm, "end": v(-6.49, -8.83) * mm});
            skLineSegment(sketch, "E371", {"start": v(-6.49, -8.83) * mm, "end": v(-6.5, -8.97) * mm});
            skLineSegment(sketch, "E372", {"start": v(-6.5, -8.97) * mm, "end": v(-6.42, -9.16) * mm});
            skLineSegment(sketch, "E373", {"start": v(-6.42, -9.16) * mm, "end": v(-6.09, -9.81) * mm});
            skLineSegment(sketch, "E374", {"start": v(-6.09, -9.81) * mm, "end": v(-5.78, -10.5) * mm});
            skLineSegment(sketch, "E375", {"start": v(-5.78, -10.5) * mm, "end": v(-5.97, -10.53) * mm});
            skLineSegment(sketch, "E376", {"start": v(-5.97, -10.53) * mm, "end": v(-6.13, -10.5) * mm});
            skLineSegment(sketch, "E377", {"start": v(-6.13, -10.5) * mm, "end": v(-6.26, -10.4) * mm});
            skLineSegment(sketch, "E378", {"start": v(-6.26, -10.4) * mm, "end": v(-6.36, -10.23) * mm});
            skLineSegment(sketch, "E379", {"start": v(-6.36, -10.23) * mm, "end": v(-6.9, -9.13) * mm});
            skLineSegment(sketch, "E380", {"start": v(-6.9, -9.13) * mm, "end": v(-7.17, -9.3) * mm});
            skLineSegment(sketch, "E381", {"start": v(-7.17, -9.3) * mm, "end": v(-7.37, -9.54) * mm});
            skLineSegment(sketch, "E382", {"start": v(-7.37, -9.54) * mm, "end": v(-7.5, -9.82) * mm});
            skLineSegment(sketch, "E383", {"start": v(-7.5, -9.82) * mm, "end": v(-7.59, -10.15) * mm});
            skLineSegment(sketch, "E384", {"start": v(-7.59, -10.15) * mm, "end": v(-7.6, -10.28) * mm});
            skLineSegment(sketch, "E385", {"start": v(-7.6, -10.28) * mm, "end": v(-7.63, -10.37) * mm});
            skLineSegment(sketch, "E386", {"start": v(-7.63, -10.37) * mm, "end": v(-7.66, -10.44) * mm});
            skLineSegment(sketch, "E387", {"start": v(-7.66, -10.44) * mm, "end": v(-7.7, -10.48) * mm});
            skLineSegment(sketch, "E388", {"start": v(-7.7, -10.48) * mm, "end": v(-7.75, -10.5) * mm});
            skLineSegment(sketch, "E389", {"start": v(-7.75, -10.5) * mm, "end": v(-7.82, -10.52) * mm});
            skLineSegment(sketch, "E390", {"start": v(-7.82, -10.52) * mm, "end": v(-7.92, -10.51) * mm});
            skLineSegment(sketch, "E391", {"start": v(-7.92, -10.51) * mm, "end": v(-8.04, -10.5) * mm});
            skLineSegment(sketch, "E392", {"start": v(-8.04, -10.5) * mm, "end": v(-7.28, -6.91) * mm});
            skLineSegment(sketch, "E393", {"start": v(-7.28, -6.91) * mm, "end": v(-7.27, -6.84) * mm});
            skLineSegment(sketch, "E394", {"start": v(-7.27, -6.84) * mm, "end": v(-7.25, -6.78) * mm});
            skLineSegment(sketch, "E395", {"start": v(-7.25, -6.78) * mm, "end": v(-7.21, -6.72) * mm});
            skLineSegment(sketch, "E396", {"start": v(-7.21, -6.72) * mm, "end": v(-7.15, -6.69) * mm});
            skLineSegment(sketch, "E397", {"start": v(-7.15, -6.69) * mm, "end": v(-7, -6.67) * mm});
            skLineSegment(sketch, "E398", {"start": v(-7, -6.67) * mm, "end": v(-6.91, -6.71) * mm});
            skLineSegment(sketch, "E399", {"start": v(-6.91, -6.71) * mm, "end": v(-6.86, -6.8) * mm});
            skLineSegment(sketch, "E400", {"start": v(-6.86, -6.8) * mm, "end": v(-6.87, -6.94) * mm});
            skLineSegment(sketch, "E401", {"start": v(-6.87, -6.94) * mm, "end": v(-7.28, -8.72) * mm});
            skLineSegment(sketch, "E402", {"start": v(-7.28, -8.72) * mm, "end": v(-7.29, -8.82) * mm});
            skLineSegment(sketch, "E403", {"start": v(-7.29, -8.82) * mm, "end": v(-7.28, -8.96) * mm});
            skLineSegment(sketch, "E404", {"start": v(-7.28, -8.96) * mm, "end": v(-6.72, -8.53) * mm});
            skLineSegment(sketch, "E405", {"start": v(-6.72, -8.53) * mm, "end": v(-6.2, -8.07) * mm});
            skLineSegment(sketch, "E406", {"start": v(-6.2, -8.07) * mm, "end": v(-6, -7.92) * mm});
            skLineSegment(sketch, "E407", {"start": v(-6, -7.92) * mm, "end": v(-5.8, -7.8) * mm});
            skLineSegment(sketch, "E408", {"start": v(-5.8, -7.8) * mm, "end": v(-5.56, -7.76) * mm});
            skLineSegment(sketch, "E409", {"start": v(-5.56, -7.76) * mm, "end": v(-5.29, -7.8) * mm});
            skLineSegment(sketch, "E410", {"start": v(-10.25, -7.7) * mm, "end": v(-9.84, -7.73) * mm});
            skLineSegment(sketch, "E411", {"start": v(-9.84, -7.73) * mm, "end": v(-9.56, -7.85) * mm});
            skLineSegment(sketch, "E412", {"start": v(-9.56, -7.85) * mm, "end": v(-9.39, -8.07) * mm});
            skLineSegment(sketch, "E413", {"start": v(-9.39, -8.07) * mm, "end": v(-9.28, -8.34) * mm});
            skLineSegment(sketch, "E414", {"start": v(-9.28, -8.34) * mm, "end": v(-9.26, -8.41) * mm});
            skLineSegment(sketch, "E415", {"start": v(-9.26, -8.41) * mm, "end": v(-9.24, -8.5) * mm});
            skLineSegment(sketch, "E416", {"start": v(-9.24, -8.5) * mm, "end": v(-9.27, -8.57) * mm});
            skLineSegment(sketch, "E417", {"start": v(-9.27, -8.57) * mm, "end": v(-9.38, -8.6) * mm});
            skLineSegment(sketch, "E418", {"start": v(-9.38, -8.6) * mm, "end": v(-9.47, -8.61) * mm});
            skLineSegment(sketch, "E419", {"start": v(-9.47, -8.61) * mm, "end": v(-9.58, -8.62) * mm});
            skLineSegment(sketch, "E420", {"start": v(-9.58, -8.62) * mm, "end": v(-9.66, -8.58) * mm});
            skLineSegment(sketch, "E421", {"start": v(-9.66, -8.58) * mm, "end": v(-9.69, -8.43) * mm});
            skLineSegment(sketch, "E422", {"start": v(-9.69, -8.43) * mm, "end": v(-9.74, -8.27) * mm});
            skLineSegment(sketch, "E423", {"start": v(-9.74, -8.27) * mm, "end": v(-9.86, -8.14) * mm});
            skLineSegment(sketch, "E424", {"start": v(-9.86, -8.14) * mm, "end": v(-10.04, -8.05) * mm});
            skLineSegment(sketch, "E425", {"start": v(-10.04, -8.05) * mm, "end": v(-10.24, -8) * mm});
            skLineSegment(sketch, "E426", {"start": v(-10.24, -8) * mm, "end": v(-10.46, -8.02) * mm});
            skLineSegment(sketch, "E427", {"start": v(-10.46, -8.02) * mm, "end": v(-10.67, -8.1) * mm});
            skLineSegment(sketch, "E428", {"start": v(-10.67, -8.1) * mm, "end": v(-10.83, -8.22) * mm});
            skLineSegment(sketch, "E429", {"start": v(-10.83, -8.22) * mm, "end": v(-10.9, -8.37) * mm});
            skLineSegment(sketch, "E430", {"start": v(-10.9, -8.37) * mm, "end": v(-10.9, -8.51) * mm});
            skLineSegment(sketch, "E431", {"start": v(-10.9, -8.51) * mm, "end": v(-10.85, -8.62) * mm});
            skLineSegment(sketch, "E432", {"start": v(-10.85, -8.62) * mm, "end": v(-10.75, -8.71) * mm});
            skLineSegment(sketch, "E433", {"start": v(-10.75, -8.71) * mm, "end": v(-10.63, -8.78) * mm});
            skLineSegment(sketch, "E434", {"start": v(-10.63, -8.78) * mm, "end": v(-9.92, -9.11) * mm});
            skLineSegment(sketch, "E435", {"start": v(-9.92, -9.11) * mm, "end": v(-9.69, -9.26) * mm});
            skLineSegment(sketch, "E436", {"start": v(-9.69, -9.26) * mm, "end": v(-9.53, -9.43) * mm});
            skLineSegment(sketch, "E437", {"start": v(-9.53, -9.43) * mm, "end": v(-9.45, -9.63) * mm});
            skLineSegment(sketch, "E438", {"start": v(-9.45, -9.63) * mm, "end": v(-9.44, -9.86) * mm});
            skLineSegment(sketch, "E439", {"start": v(-9.44, -9.86) * mm, "end": v(-9.51, -10.08) * mm});
            skLineSegment(sketch, "E440", {"start": v(-9.51, -10.08) * mm, "end": v(-9.66, -10.3) * mm});
            skLineSegment(sketch, "E441", {"start": v(-9.66, -10.3) * mm, "end": v(-9.87, -10.47) * mm});
            skLineSegment(sketch, "E442", {"start": v(-9.87, -10.47) * mm, "end": v(-10.1, -10.57) * mm});
            skLineSegment(sketch, "E443", {"start": v(-10.1, -10.57) * mm, "end": v(-10.65, -10.63) * mm});
            skLineSegment(sketch, "E444", {"start": v(-10.65, -10.63) * mm, "end": v(-11.2, -10.48) * mm});
            skLineSegment(sketch, "E445", {"start": v(-11.2, -10.48) * mm, "end": v(-11.39, -10.35) * mm});
            skLineSegment(sketch, "E446", {"start": v(-11.39, -10.35) * mm, "end": v(-11.52, -10.17) * mm});
            skLineSegment(sketch, "E447", {"start": v(-11.52, -10.17) * mm, "end": v(-11.6, -9.97) * mm});
            skLineSegment(sketch, "E448", {"start": v(-11.6, -9.97) * mm, "end": v(-11.66, -9.76) * mm});
            skLineSegment(sketch, "E449", {"start": v(-11.66, -9.76) * mm, "end": v(-11.66, -9.7) * mm});
            skLineSegment(sketch, "E450", {"start": v(-11.66, -9.7) * mm, "end": v(-11.64, -9.64) * mm});
            skLineSegment(sketch, "E451", {"start": v(-11.64, -9.64) * mm, "end": v(-11.6, -9.62) * mm});
            skLineSegment(sketch, "E452", {"start": v(-11.6, -9.62) * mm, "end": v(-11.53, -9.63) * mm});
            skLineSegment(sketch, "E453", {"start": v(-11.53, -9.63) * mm, "end": v(-11.45, -9.63) * mm});
            skLineSegment(sketch, "E454", {"start": v(-11.45, -9.63) * mm, "end": v(-11.37, -9.61) * mm});
            skLineSegment(sketch, "E455", {"start": v(-11.37, -9.61) * mm, "end": v(-11.29, -9.64) * mm});
            skLineSegment(sketch, "E456", {"start": v(-11.29, -9.64) * mm, "end": v(-11.23, -9.75) * mm});
            skLineSegment(sketch, "E457", {"start": v(-11.23, -9.75) * mm, "end": v(-11.04, -10.08) * mm});
            skLineSegment(sketch, "E458", {"start": v(-11.04, -10.08) * mm, "end": v(-10.72, -10.27) * mm});
            skLineSegment(sketch, "E459", {"start": v(-10.72, -10.27) * mm, "end": v(-10.35, -10.28) * mm});
            skLineSegment(sketch, "E460", {"start": v(-10.35, -10.28) * mm, "end": v(-10, -10.1) * mm});
            skLineSegment(sketch, "E461", {"start": v(-10, -10.1) * mm, "end": v(-9.88, -9.92) * mm});
            skLineSegment(sketch, "E462", {"start": v(-9.88, -9.92) * mm, "end": v(-9.86, -9.75) * mm});
            skLineSegment(sketch, "E463", {"start": v(-9.86, -9.75) * mm, "end": v(-9.93, -9.58) * mm});
            skLineSegment(sketch, "E464", {"start": v(-9.93, -9.58) * mm, "end": v(-10.1, -9.45) * mm});
            skLineSegment(sketch, "E465", {"start": v(-10.1, -9.45) * mm, "end": v(-10.64, -9.2) * mm});
            skLineSegment(sketch, "E466", {"start": v(-10.64, -9.2) * mm, "end": v(-11, -9.04) * mm});
            skLineSegment(sketch, "E467", {"start": v(-11, -9.04) * mm, "end": v(-11.21, -8.83) * mm});
            skLineSegment(sketch, "E468", {"start": v(-11.21, -8.83) * mm, "end": v(-11.31, -8.57) * mm});
            skLineSegment(sketch, "E469", {"start": v(-11.31, -8.57) * mm, "end": v(-11.3, -8.26) * mm});
            skLineSegment(sketch, "E470", {"start": v(-11.3, -8.26) * mm, "end": v(-11.2, -8.04) * mm});
            skLineSegment(sketch, "E471", {"start": v(-11.2, -8.04) * mm, "end": v(-10.99, -7.86) * mm});
            skLineSegment(sketch, "E472", {"start": v(-10.99, -7.86) * mm, "end": v(-10.7, -7.75) * mm});
            skLineSegment(sketch, "E473", {"start": v(-10.7, -7.75) * mm, "end": v(-10.37, -7.7) * mm});
            skLineSegment(sketch, "E474", {"start": v(-10.37, -7.7) * mm, "end": v(-10.25, -7.7) * mm});
            skLineSegment(sketch, "E475", {"start": v(-3.36, -9.93) * mm, "end": v(-2.4, -8.13) * mm});
            skLineSegment(sketch, "E476", {"start": v(-2.4, -8.13) * mm, "end": v(-2.3, -7.95) * mm});
            skLineSegment(sketch, "E477", {"start": v(-2.3, -7.95) * mm, "end": v(-2.17, -7.82) * mm});
            skLineSegment(sketch, "E478", {"start": v(-2.17, -7.82) * mm, "end": v(-2, -7.76) * mm});
            skLineSegment(sketch, "E479", {"start": v(-2, -7.76) * mm, "end": v(-1.76, -7.8) * mm});
            skLineSegment(sketch, "E480", {"start": v(-1.76, -7.8) * mm, "end": v(-3.2, -10.3) * mm});
            skLineSegment(sketch, "E481", {"start": v(-3.2, -10.3) * mm, "end": v(-3.73, -11.2) * mm});
            skLineSegment(sketch, "E482", {"start": v(-3.73, -11.2) * mm, "end": v(-3.9, -11.39) * mm});
            skLineSegment(sketch, "E483", {"start": v(-3.9, -11.39) * mm, "end": v(-4.12, -11.5) * mm});
            skLineSegment(sketch, "E484", {"start": v(-4.12, -11.5) * mm, "end": v(-4.37, -11.56) * mm});
            skLineSegment(sketch, "E485", {"start": v(-4.37, -11.56) * mm, "end": v(-4.62, -11.54) * mm});
            skLineSegment(sketch, "E486", {"start": v(-4.62, -11.54) * mm, "end": v(-4.68, -11.52) * mm});
            skLineSegment(sketch, "E487", {"start": v(-4.68, -11.52) * mm, "end": v(-4.7, -11.48) * mm});
            skLineSegment(sketch, "E488", {"start": v(-4.7, -11.48) * mm, "end": v(-4.71, -11.44) * mm});
            skLineSegment(sketch, "E489", {"start": v(-4.71, -11.44) * mm, "end": v(-4.7, -11.4) * mm});
            skLineSegment(sketch, "E490", {"start": v(-4.7, -11.4) * mm, "end": v(-4.68, -11.3) * mm});
            skLineSegment(sketch, "E491", {"start": v(-4.68, -11.3) * mm, "end": v(-4.65, -11.23) * mm});
            skLineSegment(sketch, "E492", {"start": v(-4.65, -11.23) * mm, "end": v(-4.59, -11.19) * mm});
            skLineSegment(sketch, "E493", {"start": v(-4.59, -11.19) * mm, "end": v(-4.49, -11.18) * mm});
            skLineSegment(sketch, "E494", {"start": v(-4.49, -11.18) * mm, "end": v(-4.3, -11.18) * mm});
            skLineSegment(sketch, "E495", {"start": v(-4.3, -11.18) * mm, "end": v(-4.16, -11.11) * mm});
            skLineSegment(sketch, "E496", {"start": v(-4.16, -11.11) * mm, "end": v(-4.04, -11) * mm});
            skLineSegment(sketch, "E497", {"start": v(-4.04, -11) * mm, "end": v(-3.91, -10.87) * mm});
            skLineSegment(sketch, "E498", {"start": v(-3.91, -10.87) * mm, "end": v(-3.75, -10.59) * mm});
            skLineSegment(sketch, "E499", {"start": v(-3.75, -10.59) * mm, "end": v(-3.73, -10.3) * mm});
            skLineSegment(sketch, "E500", {"start": v(-3.73, -10.3) * mm, "end": v(-3.78, -10.03) * mm});
            skLineSegment(sketch, "E501", {"start": v(-3.78, -10.03) * mm, "end": v(-3.84, -9.75) * mm});
            skLineSegment(sketch, "E502", {"start": v(-3.84, -9.75) * mm, "end": v(-4.16, -8.01) * mm});
            skLineSegment(sketch, "E503", {"start": v(-4.16, -8.01) * mm, "end": v(-4.18, -7.94) * mm});
            skLineSegment(sketch, "E504", {"start": v(-4.18, -7.94) * mm, "end": v(-4.19, -7.86) * mm});
            skLineSegment(sketch, "E505", {"start": v(-4.19, -7.86) * mm, "end": v(-4.16, -7.8) * mm});
            skLineSegment(sketch, "E506", {"start": v(-4.16, -7.8) * mm, "end": v(-4.06, -7.77) * mm});
            skLineSegment(sketch, "E507", {"start": v(-4.06, -7.77) * mm, "end": v(-3.96, -7.76) * mm});
            skLineSegment(sketch, "E508", {"start": v(-3.96, -7.76) * mm, "end": v(-3.86, -7.77) * mm});
            skLineSegment(sketch, "E509", {"start": v(-3.86, -7.77) * mm, "end": v(-3.79, -7.82) * mm});
            skLineSegment(sketch, "E510", {"start": v(-3.79, -7.82) * mm, "end": v(-3.74, -7.94) * mm});
            skLineSegment(sketch, "E511", {"start": v(-3.74, -7.94) * mm, "end": v(-3.43, -9.91) * mm});
            skLineSegment(sketch, "E512", {"start": v(-3.43, -9.91) * mm, "end": v(-3.36, -9.93) * mm});
            skLineSegment(sketch, "E513", {"start": v(7.93, -7.78) * mm, "end": v(7.28, -8.99) * mm});
            skLineSegment(sketch, "E514", {"start": v(7.28, -8.99) * mm, "end": v(6.53, -10.3) * mm});
            skLineSegment(sketch, "E515", {"start": v(6.53, -10.3) * mm, "end": v(6.47, -10.39) * mm});
            skLineSegment(sketch, "E516", {"start": v(6.47, -10.39) * mm, "end": v(6.4, -10.46) * mm});
            skLineSegment(sketch, "E517", {"start": v(6.4, -10.46) * mm, "end": v(6.32, -10.5) * mm});
            skLineSegment(sketch, "E518", {"start": v(6.32, -10.5) * mm, "end": v(6.2, -10.53) * mm});
            skLineSegment(sketch, "E519", {"start": v(6.2, -10.53) * mm, "end": v(6.07, -10.52) * mm});
            skLineSegment(sketch, "E520", {"start": v(6.07, -10.52) * mm, "end": v(5.99, -10.47) * mm});
            skLineSegment(sketch, "E521", {"start": v(5.99, -10.47) * mm, "end": v(5.94, -10.4) * mm});
            skLineSegment(sketch, "E522", {"start": v(5.94, -10.4) * mm, "end": v(5.91, -10.3) * mm});
            skLineSegment(sketch, "E523", {"start": v(5.91, -10.3) * mm, "end": v(5.6, -8.25) * mm});
            skLineSegment(sketch, "E524", {"start": v(5.6, -8.25) * mm, "end": v(5.57, -8.05) * mm});
            skLineSegment(sketch, "E525", {"start": v(5.57, -8.05) * mm, "end": v(5.55, -7.96) * mm});
            skLineSegment(sketch, "E526", {"start": v(5.55, -7.96) * mm, "end": v(5.53, -7.87) * mm});
            skLineSegment(sketch, "E527", {"start": v(5.53, -7.87) * mm, "end": v(5.56, -7.8) * mm});
            skLineSegment(sketch, "E528", {"start": v(5.56, -7.8) * mm, "end": v(5.67, -7.77) * mm});
            skLineSegment(sketch, "E529", {"start": v(5.67, -7.77) * mm, "end": v(5.78, -7.76) * mm});
            skLineSegment(sketch, "E530", {"start": v(5.78, -7.76) * mm, "end": v(5.87, -7.77) * mm});
            skLineSegment(sketch, "E531", {"start": v(5.87, -7.77) * mm, "end": v(5.94, -7.83) * mm});
            skLineSegment(sketch, "E532", {"start": v(5.94, -7.83) * mm, "end": v(5.98, -7.98) * mm});
            skLineSegment(sketch, "E533", {"start": v(5.98, -7.98) * mm, "end": v(6.21, -9.8) * mm});
            skLineSegment(sketch, "E534", {"start": v(6.21, -9.8) * mm, "end": v(6.24, -9.89) * mm});
            skLineSegment(sketch, "E535", {"start": v(6.24, -9.89) * mm, "end": v(6.29, -9.97) * mm});
            skLineSegment(sketch, "E536", {"start": v(6.29, -9.97) * mm, "end": v(7.34, -8.05) * mm});
            skLineSegment(sketch, "E537", {"start": v(7.34, -8.05) * mm, "end": v(7.45, -7.88) * mm});
            skLineSegment(sketch, "E538", {"start": v(7.45, -7.88) * mm, "end": v(7.58, -7.79) * mm});
            skLineSegment(sketch, "E539", {"start": v(7.58, -7.79) * mm, "end": v(7.74, -7.76) * mm});
            skLineSegment(sketch, "E540", {"start": v(7.74, -7.76) * mm, "end": v(7.93, -7.78) * mm});
            skLineSegment(sketch, "E541", {"start": v(3.41, -10.52) * mm, "end": v(3.3, -10.52) * mm});
            skLineSegment(sketch, "E542", {"start": v(3.3, -10.52) * mm, "end": v(3.24, -10.5) * mm});
            skLineSegment(sketch, "E543", {"start": v(3.24, -10.5) * mm, "end": v(3.23, -10.42) * mm});
            skLineSegment(sketch, "E544", {"start": v(3.23, -10.42) * mm, "end": v(3.25, -10.3) * mm});
            skLineSegment(sketch, "E545", {"start": v(3.25, -10.3) * mm, "end": v(3.74, -7.94) * mm});
            skLineSegment(sketch, "E546", {"start": v(3.74, -7.94) * mm, "end": v(3.79, -7.82) * mm});
            skLineSegment(sketch, "E547", {"start": v(3.79, -7.82) * mm, "end": v(3.86, -7.77) * mm});
            skLineSegment(sketch, "E548", {"start": v(3.86, -7.77) * mm, "end": v(3.95, -7.76) * mm});
            skLineSegment(sketch, "E549", {"start": v(3.95, -7.76) * mm, "end": v(4.05, -7.77) * mm});
            skLineSegment(sketch, "E550", {"start": v(4.05, -7.77) * mm, "end": v(4.16, -7.8) * mm});
            skLineSegment(sketch, "E551", {"start": v(4.16, -7.8) * mm, "end": v(4.19, -7.86) * mm});
            skLineSegment(sketch, "E552", {"start": v(4.19, -7.86) * mm, "end": v(4.18, -7.94) * mm});
            skLineSegment(sketch, "E553", {"start": v(4.18, -7.94) * mm, "end": v(4.16, -8) * mm});
            skLineSegment(sketch, "E554", {"start": v(4.16, -8) * mm, "end": v(3.64, -10.35) * mm});
            skLineSegment(sketch, "E555", {"start": v(3.64, -10.35) * mm, "end": v(3.6, -10.45) * mm});
            skLineSegment(sketch, "E556", {"start": v(3.6, -10.45) * mm, "end": v(3.56, -10.5) * mm});
            skLineSegment(sketch, "E557", {"start": v(3.56, -10.5) * mm, "end": v(3.5, -10.52) * mm});
            skLineSegment(sketch, "E558", {"start": v(3.5, -10.52) * mm, "end": v(3.41, -10.52) * mm});
            skLineSegment(sketch, "E559", {"start": v(4.1, -7.28) * mm, "end": v(4, -7.29) * mm});
            skLineSegment(sketch, "E560", {"start": v(4, -7.29) * mm, "end": v(3.95, -7.25) * mm});
            skLineSegment(sketch, "E561", {"start": v(3.95, -7.25) * mm, "end": v(3.93, -7.2) * mm});
            skLineSegment(sketch, "E562", {"start": v(3.93, -7.2) * mm, "end": v(3.93, -7.1) * mm});
            skLineSegment(sketch, "E563", {"start": v(3.93, -7.1) * mm, "end": v(3.96, -6.89) * mm});
            skLineSegment(sketch, "E564", {"start": v(3.96, -6.89) * mm, "end": v(4.03, -6.75) * mm});
            skLineSegment(sketch, "E565", {"start": v(4.03, -6.75) * mm, "end": v(4.14, -6.69) * mm});
            skLineSegment(sketch, "E566", {"start": v(4.14, -6.69) * mm, "end": v(4.3, -6.69) * mm});
            skLineSegment(sketch, "E567", {"start": v(4.3, -6.69) * mm, "end": v(4.36, -6.7) * mm});
            skLineSegment(sketch, "E568", {"start": v(4.36, -6.7) * mm, "end": v(4.4, -6.72) * mm});
            skLineSegment(sketch, "E569", {"start": v(4.4, -6.72) * mm, "end": v(4.33, -7.2) * mm});
            skLineSegment(sketch, "E570", {"start": v(4.33, -7.2) * mm, "end": v(4.3, -7.26) * mm});
            skLineSegment(sketch, "E571", {"start": v(4.3, -7.26) * mm, "end": v(4.23, -7.28) * mm});
            skLineSegment(sketch, "E572", {"start": v(4.23, -7.28) * mm, "end": v(4.17, -7.29) * mm});
            skLineSegment(sketch, "E573", {"start": v(4.17, -7.29) * mm, "end": v(4.1, -7.28) * mm});
            skLineSegment(sketch, "E574", {"start": v(6.33, -13.43) * mm, "end": v(6.22, -14.12) * mm});
            skLineSegment(sketch, "E575", {"start": v(6.22, -14.12) * mm, "end": v(5.86, -14.67) * mm});
            skLineSegment(sketch, "E576", {"start": v(5.86, -14.67) * mm, "end": v(5.64, -14.82) * mm});
            skLineSegment(sketch, "E577", {"start": v(5.64, -14.82) * mm, "end": v(5.4, -14.9) * mm});
            skLineSegment(sketch, "E578", {"start": v(5.4, -14.9) * mm, "end": v(5.15, -14.88) * mm});
            skLineSegment(sketch, "E579", {"start": v(5.15, -14.88) * mm, "end": v(4.9, -14.78) * mm});
            skLineSegment(sketch, "E580", {"start": v(4.9, -14.78) * mm, "end": v(4.75, -14.63) * mm});
            skLineSegment(sketch, "E581", {"start": v(4.75, -14.63) * mm, "end": v(4.65, -14.43) * mm});
            skLineSegment(sketch, "E582", {"start": v(4.65, -14.43) * mm, "end": v(4.6, -14.18) * mm});
            skLineSegment(sketch, "E583", {"start": v(4.6, -14.18) * mm, "end": v(4.61, -13.93) * mm});
            skLineSegment(sketch, "E584", {"start": v(4.61, -13.93) * mm, "end": v(4.76, -13.43) * mm});
            skLineSegment(sketch, "E585", {"start": v(4.76, -13.43) * mm, "end": v(5, -12.98) * mm});
            skLineSegment(sketch, "E586", {"start": v(5, -12.98) * mm, "end": v(5.22, -12.78) * mm});
            skLineSegment(sketch, "E587", {"start": v(5.22, -12.78) * mm, "end": v(5.5, -12.66) * mm});
            skLineSegment(sketch, "E588", {"start": v(5.5, -12.66) * mm, "end": v(5.79, -12.65) * mm});
            skLineSegment(sketch, "E589", {"start": v(5.79, -12.65) * mm, "end": v(6.05, -12.75) * mm});
            skLineSegment(sketch, "E590", {"start": v(6.05, -12.75) * mm, "end": v(6.2, -12.9) * mm});
            skLineSegment(sketch, "E591", {"start": v(6.2, -12.9) * mm, "end": v(6.3, -13.07) * mm});
            skLineSegment(sketch, "E592", {"start": v(6.3, -13.07) * mm, "end": v(6.33, -13.25) * mm});
            skLineSegment(sketch, "E593", {"start": v(6.33, -13.25) * mm, "end": v(6.33, -13.43) * mm});
            skLineSegment(sketch, "E594", {"start": v(-10.43, -13.34) * mm, "end": v(-10.28, -13.1) * mm});
            skLineSegment(sketch, "E595", {"start": v(-10.28, -13.1) * mm, "end": v(-10.12, -12.9) * mm});
            skLineSegment(sketch, "E596", {"start": v(-10.12, -12.9) * mm, "end": v(-9.92, -12.74) * mm});
            skLineSegment(sketch, "E597", {"start": v(-9.92, -12.74) * mm, "end": v(-9.68, -12.64) * mm});
            skLineSegment(sketch, "E598", {"start": v(-9.68, -12.64) * mm, "end": v(-9.5, -12.62) * mm});
            skLineSegment(sketch, "E599", {"start": v(-9.5, -12.62) * mm, "end": v(-9.34, -12.63) * mm});
            skLineSegment(sketch, "E600", {"start": v(-9.34, -12.63) * mm, "end": v(-9.19, -12.69) * mm});
            skLineSegment(sketch, "E601", {"start": v(-9.19, -12.69) * mm, "end": v(-9.05, -12.77) * mm});
            skLineSegment(sketch, "E602", {"start": v(-9.05, -12.77) * mm, "end": v(-8.95, -12.86) * mm});
            skLineSegment(sketch, "E603", {"start": v(-8.95, -12.86) * mm, "end": v(-8.87, -12.98) * mm});
            skLineSegment(sketch, "E604", {"start": v(-8.87, -12.98) * mm, "end": v(-8.84, -13.12) * mm});
            skLineSegment(sketch, "E605", {"start": v(-8.84, -13.12) * mm, "end": v(-8.85, -13.26) * mm});
            skLineSegment(sketch, "E606", {"start": v(-8.85, -13.26) * mm, "end": v(-8.91, -13.34) * mm});
            skLineSegment(sketch, "E607", {"start": v(-8.91, -13.34) * mm, "end": v(-9, -13.36) * mm});
            skLineSegment(sketch, "E608", {"start": v(-9, -13.36) * mm, "end": v(-9.11, -13.34) * mm});
            skLineSegment(sketch, "E609", {"start": v(-9.11, -13.34) * mm, "end": v(-9.21, -13.33) * mm});
            skLineSegment(sketch, "E610", {"start": v(-9.21, -13.33) * mm, "end": v(-10.43, -13.34) * mm});
            skLineSegment(sketch, "E611", {"start": v(8.84, -13.34) * mm, "end": v(9.05, -12.98) * mm});
            skLineSegment(sketch, "E612", {"start": v(9.05, -12.98) * mm, "end": v(9.35, -12.74) * mm});
            skLineSegment(sketch, "E613", {"start": v(9.35, -12.74) * mm, "end": v(9.68, -12.63) * mm});
            skLineSegment(sketch, "E614", {"start": v(9.68, -12.63) * mm, "end": v(10.02, -12.67) * mm});
            skLineSegment(sketch, "E615", {"start": v(10.02, -12.67) * mm, "end": v(10.23, -12.8) * mm});
            skLineSegment(sketch, "E616", {"start": v(10.23, -12.8) * mm, "end": v(10.35, -13) * mm});
            skLineSegment(sketch, "E617", {"start": v(10.35, -13) * mm, "end": v(10.4, -13.18) * mm});
            skLineSegment(sketch, "E618", {"start": v(10.4, -13.18) * mm, "end": v(10.4, -13.28) * mm});
            skLineSegment(sketch, "E619", {"start": v(10.4, -13.28) * mm, "end": v(10.32, -13.33) * mm});
            skLineSegment(sketch, "E620", {"start": v(10.32, -13.33) * mm, "end": v(10.16, -13.34) * mm});
            skLineSegment(sketch, "E621", {"start": v(10.16, -13.34) * mm, "end": v(8.84, -13.34) * mm});
            skLineSegment(sketch, "E622", {"start": v(0.39, -13.97) * mm, "end": v(0.43, -13.7) * mm});
            skLineSegment(sketch, "E623", {"start": v(0.43, -13.7) * mm, "end": v(0.5, -13.42) * mm});
            skLineSegment(sketch, "E624", {"start": v(0.5, -13.42) * mm, "end": v(0.65, -13.14) * mm});
            skLineSegment(sketch, "E625", {"start": v(0.65, -13.14) * mm, "end": v(0.87, -12.89) * mm});
            skLineSegment(sketch, "E626", {"start": v(0.87, -12.89) * mm, "end": v(1.06, -12.74) * mm});
            skLineSegment(sketch, "E627", {"start": v(1.06, -12.74) * mm, "end": v(1.26, -12.65) * mm});
            skLineSegment(sketch, "E628", {"start": v(1.26, -12.65) * mm, "end": v(1.47, -12.63) * mm});
            skLineSegment(sketch, "E629", {"start": v(1.47, -12.63) * mm, "end": v(1.71, -12.68) * mm});
            skLineSegment(sketch, "E630", {"start": v(1.71, -12.68) * mm, "end": v(1.9, -12.8) * mm});
            skLineSegment(sketch, "E631", {"start": v(1.9, -12.8) * mm, "end": v(2.03, -12.96) * mm});
            skLineSegment(sketch, "E632", {"start": v(2.03, -12.96) * mm, "end": v(2.1, -13.15) * mm});
            skLineSegment(sketch, "E633", {"start": v(2.1, -13.15) * mm, "end": v(2.12, -13.35) * mm});
            skLineSegment(sketch, "E634", {"start": v(2.12, -13.35) * mm, "end": v(2.03, -14.02) * mm});
            skLineSegment(sketch, "E635", {"start": v(2.03, -14.02) * mm, "end": v(1.68, -14.6) * mm});
            skLineSegment(sketch, "E636", {"start": v(1.68, -14.6) * mm, "end": v(1.47, -14.78) * mm});
            skLineSegment(sketch, "E637", {"start": v(1.47, -14.78) * mm, "end": v(1.26, -14.88) * mm});
            skLineSegment(sketch, "E638", {"start": v(1.26, -14.88) * mm, "end": v(1.06, -14.9) * mm});
            skLineSegment(sketch, "E639", {"start": v(1.06, -14.9) * mm, "end": v(0.85, -14.85) * mm});
            skLineSegment(sketch, "E640", {"start": v(0.85, -14.85) * mm, "end": v(0.64, -14.72) * mm});
            skLineSegment(sketch, "E641", {"start": v(0.64, -14.72) * mm, "end": v(0.5, -14.55) * mm});
            skLineSegment(sketch, "E642", {"start": v(0.5, -14.55) * mm, "end": v(0.41, -14.3) * mm});
            skLineSegment(sketch, "E643", {"start": v(0.41, -14.3) * mm, "end": v(0.39, -13.97) * mm});
            skLineSegment(sketch, "E644", {"start": v(-0.39, -9.46) * mm, "end": v(-0.33, -9.04) * mm});
            skLineSegment(sketch, "E645", {"start": v(-0.33, -9.04) * mm, "end": v(-0.15, -8.62) * mm});
            skLineSegment(sketch, "E646", {"start": v(-0.15, -8.62) * mm, "end": v(0.13, -8.26) * mm});
            skLineSegment(sketch, "E647", {"start": v(0.13, -8.26) * mm, "end": v(0.49, -8.05) * mm});
            skLineSegment(sketch, "E648", {"start": v(0.49, -8.05) * mm, "end": v(0.86, -8.04) * mm});
            skLineSegment(sketch, "E649", {"start": v(0.86, -8.04) * mm, "end": v(1.18, -8.18) * mm});
            skLineSegment(sketch, "E650", {"start": v(1.18, -8.18) * mm, "end": v(1.4, -8.45) * mm});
            skLineSegment(sketch, "E651", {"start": v(1.4, -8.45) * mm, "end": v(1.46, -8.8) * mm});
            skLineSegment(sketch, "E652", {"start": v(1.46, -8.8) * mm, "end": v(1.32, -9.44) * mm});
            skLineSegment(sketch, "E653", {"start": v(1.32, -9.44) * mm, "end": v(0.95, -10) * mm});
            skLineSegment(sketch, "E654", {"start": v(0.95, -10) * mm, "end": v(0.75, -10.15) * mm});
            skLineSegment(sketch, "E655", {"start": v(0.75, -10.15) * mm, "end": v(0.55, -10.25) * mm});
            skLineSegment(sketch, "E656", {"start": v(0.55, -10.25) * mm, "end": v(0.32, -10.29) * mm});
            skLineSegment(sketch, "E657", {"start": v(0.32, -10.29) * mm, "end": v(0.08, -10.24) * mm});
            skLineSegment(sketch, "E658", {"start": v(0.08, -10.24) * mm, "end": v(-0.15, -10.12) * mm});
            skLineSegment(sketch, "E659", {"start": v(-0.15, -10.12) * mm, "end": v(-0.3, -9.97) * mm});
            skLineSegment(sketch, "E660", {"start": v(-0.3, -9.97) * mm, "end": v(-0.37, -9.75) * mm});
            skLineSegment(sketch, "E661", {"start": v(-0.37, -9.75) * mm, "end": v(-0.39, -9.46) * mm});
            skLineSegment(sketch, "E662", {"start": v(9.46, -8.9) * mm, "end": v(9.6, -8.6) * mm});
            skLineSegment(sketch, "E663", {"start": v(9.6, -8.6) * mm, "end": v(9.77, -8.35) * mm});
            skLineSegment(sketch, "E664", {"start": v(9.77, -8.35) * mm, "end": v(10, -8.15) * mm});
            skLineSegment(sketch, "E665", {"start": v(10, -8.15) * mm, "end": v(10.3, -8.02) * mm});
            skLineSegment(sketch, "E666", {"start": v(10.3, -8.02) * mm, "end": v(10.46, -8) * mm});
            skLineSegment(sketch, "E667", {"start": v(10.46, -8) * mm, "end": v(10.62, -8.03) * mm});
            skLineSegment(sketch, "E668", {"start": v(10.62, -8.03) * mm, "end": v(10.78, -8.1) * mm});
            skLineSegment(sketch, "E669", {"start": v(10.78, -8.1) * mm, "end": v(10.92, -8.21) * mm});
            skLineSegment(sketch, "E670", {"start": v(10.92, -8.21) * mm, "end": v(11.04, -8.34) * mm});
            skLineSegment(sketch, "E671", {"start": v(11.04, -8.34) * mm, "end": v(11.13, -8.5) * mm});
            skLineSegment(sketch, "E672", {"start": v(11.13, -8.5) * mm, "end": v(11.18, -8.65) * mm});
            skLineSegment(sketch, "E673", {"start": v(11.18, -8.65) * mm, "end": v(11.18, -8.81) * mm});
            skLineSegment(sketch, "E674", {"start": v(11.18, -8.81) * mm, "end": v(11.16, -8.88) * mm});
            skLineSegment(sketch, "E675", {"start": v(11.16, -8.88) * mm, "end": v(11.11, -8.9) * mm});
            skLineSegment(sketch, "E676", {"start": v(11.11, -8.9) * mm, "end": v(11.06, -8.9) * mm});
            skLineSegment(sketch, "E677", {"start": v(11.06, -8.9) * mm, "end": v(11, -8.9) * mm});
            skLineSegment(sketch, "E678", {"start": v(11, -8.9) * mm, "end": v(9.46, -8.9) * mm});
            skSolve(sketch);
        }
        {
            var Q0;
            Q0 = qSketchRegion(id + "F5", true);
            extrude(context, id + "F6", {"entities" : qUnion([Q0]), "operationType" : NewBodyOperationType.ADD, "depth" : 0.5 * mm});
        }
        {
            var Q0;
            Q0=makeQuery(id+"F1.opExtrude","CAP_FACE",FACE,{"disambiguationData":[OSD([sQuery(id+"F0.wireOp",EDGE,"E0"),sQuery(id+"F0.wireOp",EDGE,"E1"),sQuery(id+"F0.wireOp",EDGE,"E2"),sQuery(id+"F0.wireOp",EDGE,"E3"),sQuery(id+"F0.wireOp",EDGE,"E4")])],"isStart":false});
            var sketch = newSketch(context, id + "F7", { "sketchPlane" : qUnion([Q0])});
            skLineSegment(sketch, "E679", {"start": v(-3.45, 17.3) * mm, "end": v(-4.7, 16.33) * mm});
            skLineSegment(sketch, "E680", {"start": v(-4.7, 16.33) * mm, "end": v(-5.6, 15.54) * mm});
            skLineSegment(sketch, "E681", {"start": v(-5.6, 15.54) * mm, "end": v(-6.41, 14.68) * mm});
            skLineSegment(sketch, "E682", {"start": v(-6.41, 14.68) * mm, "end": v(-7.5, 13.27) * mm});
            skLineSegment(sketch, "E683", {"start": v(-7.5, 13.27) * mm, "end": v(-8.28, 12) * mm});
            skLineSegment(sketch, "E684", {"start": v(-8.28, 12) * mm, "end": v(-8.9, 10.66) * mm});
            skLineSegment(sketch, "E685", {"start": v(-8.9, 10.66) * mm, "end": v(-9.38, 9.23) * mm});
            skLineSegment(sketch, "E686", {"start": v(-9.38, 9.23) * mm, "end": v(-9.67, 7.75) * mm});
            skLineSegment(sketch, "E687", {"start": v(-9.67, 7.75) * mm, "end": v(-9.75, 6.45) * mm});
            skLineSegment(sketch, "E688", {"start": v(-9.75, 6.45) * mm, "end": v(-9.7, 5.14) * mm});
            skLineSegment(sketch, "E689", {"start": v(-9.7, 5.14) * mm, "end": v(-9.47, 3.73) * mm});
            skLineSegment(sketch, "E690", {"start": v(-9.47, 3.73) * mm, "end": v(-9.08, 2.36) * mm});
            skLineSegment(sketch, "E691", {"start": v(-9.08, 2.36) * mm, "end": v(-8.27, 0.56) * mm});
            skLineSegment(sketch, "E692", {"start": v(-8.27, 0.56) * mm, "end": v(-7.17, -1.08) * mm});
            skLineSegment(sketch, "E693", {"start": v(-7.17, -1.08) * mm, "end": v(-6.31, -2.05) * mm});
            skLineSegment(sketch, "E694", {"start": v(-6.31, -2.05) * mm, "end": v(-5.37, -2.91) * mm});
            skLineSegment(sketch, "E695", {"start": v(-5.37, -2.91) * mm, "end": v(-4.35, -3.68) * mm});
            skLineSegment(sketch, "E696", {"start": v(-4.35, -3.68) * mm, "end": v(-3.25, -4.36) * mm});
            skLineSegment(sketch, "E697", {"start": v(-3.25, -4.36) * mm, "end": v(-1.35, -5.24) * mm});
            skLineSegment(sketch, "E698", {"start": v(-1.35, -5.24) * mm, "end": v(0.66, -5.85) * mm});
            skLineSegment(sketch, "E699", {"start": v(0.66, -5.85) * mm, "end": v(0.8, -5.9) * mm});
            skLineSegment(sketch, "E700", {"start": v(0.8, -5.9) * mm, "end": v(0.85, -5.93) * mm});
            skLineSegment(sketch, "E701", {"start": v(0.85, -5.93) * mm, "end": v(0.86, -5.98) * mm});
            skLineSegment(sketch, "E702", {"start": v(0.86, -5.98) * mm, "end": v(-0.23, -6) * mm});
            skLineSegment(sketch, "E703", {"start": v(-0.23, -6) * mm, "end": v(-1.43, -5.88) * mm});
            skLineSegment(sketch, "E704", {"start": v(-1.43, -5.88) * mm, "end": v(-2.68, -5.61) * mm});
            skLineSegment(sketch, "E705", {"start": v(-2.68, -5.61) * mm, "end": v(-3.97, -5.19) * mm});
            skLineSegment(sketch, "E706", {"start": v(-3.97, -5.19) * mm, "end": v(-5.26, -4.6) * mm});
            skLineSegment(sketch, "E707", {"start": v(-5.26, -4.6) * mm, "end": v(-6.52, -3.83) * mm});
            skLineSegment(sketch, "E708", {"start": v(-6.52, -3.83) * mm, "end": v(-7.72, -2.88) * mm});
            skLineSegment(sketch, "E709", {"start": v(-7.72, -2.88) * mm, "end": v(-8.82, -1.73) * mm});
            skLineSegment(sketch, "E710", {"start": v(-8.82, -1.73) * mm, "end": v(-9.87, -0.31) * mm});
            skLineSegment(sketch, "E711", {"start": v(-9.87, -0.31) * mm, "end": v(-10.67, 1.14) * mm});
            skLineSegment(sketch, "E712", {"start": v(-10.67, 1.14) * mm, "end": v(-11.25, 2.64) * mm});
            skLineSegment(sketch, "E713", {"start": v(-11.25, 2.64) * mm, "end": v(-11.6, 4.17) * mm});
            skLineSegment(sketch, "E714", {"start": v(-11.6, 4.17) * mm, "end": v(-11.71, 5.74) * mm});
            skLineSegment(sketch, "E715", {"start": v(-11.71, 5.74) * mm, "end": v(-11.6, 7.35) * mm});
            skLineSegment(sketch, "E716", {"start": v(-11.6, 7.35) * mm, "end": v(-11.27, 8.98) * mm});
            skLineSegment(sketch, "E717", {"start": v(-11.27, 8.98) * mm, "end": v(-10.71, 10.65) * mm});
            skLineSegment(sketch, "E718", {"start": v(-10.71, 10.65) * mm, "end": v(-10.28, 11.6) * mm});
            skLineSegment(sketch, "E719", {"start": v(-10.28, 11.6) * mm, "end": v(-9.76, 12.5) * mm});
            skLineSegment(sketch, "E720", {"start": v(-9.76, 12.5) * mm, "end": v(-9.16, 13.35) * mm});
            skLineSegment(sketch, "E721", {"start": v(-9.16, 13.35) * mm, "end": v(-8.48, 14.15) * mm});
            skLineSegment(sketch, "E722", {"start": v(-8.48, 14.15) * mm, "end": v(-7.62, 15) * mm});
            skLineSegment(sketch, "E723", {"start": v(-7.62, 15) * mm, "end": v(-6.68, 15.75) * mm});
            skLineSegment(sketch, "E724", {"start": v(-6.68, 15.75) * mm, "end": v(-5.68, 16.4) * mm});
            skLineSegment(sketch, "E725", {"start": v(-5.68, 16.4) * mm, "end": v(-4.6, 16.95) * mm});
            skLineSegment(sketch, "E726", {"start": v(-4.6, 16.95) * mm, "end": v(-4.04, 17.18) * mm});
            skLineSegment(sketch, "E727", {"start": v(-4.04, 17.18) * mm, "end": v(-3.45, 17.3) * mm});
            skSolve(sketch);
        }
        {
            var Q0;
            Q0 = qSketchRegion(id + "F7", true);
            extrude(context, id + "F8", {"entities" : qUnion([Q0]), "operationType" : NewBodyOperationType.ADD, "depth" : 1 * mm});
        }
        {
            var Q0;
            Q0=makeQuery(id+"F1.opExtrude","CAP_FACE",FACE,{"disambiguationData":[OSD([sQuery(id+"F0.wireOp",EDGE,"E0"),sQuery(id+"F0.wireOp",EDGE,"E1"),sQuery(id+"F0.wireOp",EDGE,"E2"),sQuery(id+"F0.wireOp",EDGE,"E3"),sQuery(id+"F0.wireOp",EDGE,"E4")])],"isStart":false});
            var sketch = newSketch(context, id + "F9", { "sketchPlane" : qUnion([Q0])});
            skLineSegment(sketch, "E728", {"start": v(-1.93, -3.81) * mm, "end": v(-3.04, -3.1) * mm});
            skLineSegment(sketch, "E729", {"start": v(-3.04, -3.1) * mm, "end": v(-4.32, -2.1) * mm});
            skLineSegment(sketch, "E730", {"start": v(-4.32, -2.1) * mm, "end": v(-5.47, -0.97) * mm});
            skLineSegment(sketch, "E731", {"start": v(-5.47, -0.97) * mm, "end": v(-6.25, -0.01) * mm});
            skLineSegment(sketch, "E732", {"start": v(-6.25, -0.01) * mm, "end": v(-6.92, 1.03) * mm});
            skLineSegment(sketch, "E733", {"start": v(-6.92, 1.03) * mm, "end": v(-7.58, 2.48) * mm});
            skLineSegment(sketch, "E734", {"start": v(-7.58, 2.48) * mm, "end": v(-7.99, 4.02) * mm});
            skLineSegment(sketch, "E735", {"start": v(-7.99, 4.02) * mm, "end": v(-8.05, 4.58) * mm});
            skLineSegment(sketch, "E736", {"start": v(-8.05, 4.58) * mm, "end": v(-8.07, 5.14) * mm});
            skLineSegment(sketch, "E737", {"start": v(-8.07, 5.14) * mm, "end": v(-8.08, 6.08) * mm});
            skLineSegment(sketch, "E738", {"start": v(-8.08, 6.08) * mm, "end": v(-7.98, 7) * mm});
            skLineSegment(sketch, "E739", {"start": v(-7.98, 7) * mm, "end": v(-7.79, 7.9) * mm});
            skLineSegment(sketch, "E740", {"start": v(-7.79, 7.9) * mm, "end": v(-7.51, 8.8) * mm});
            skLineSegment(sketch, "E741", {"start": v(-7.51, 8.8) * mm, "end": v(-7.16, 9.67) * mm});
            skLineSegment(sketch, "E742", {"start": v(-7.16, 9.67) * mm, "end": v(-6.73, 10.5) * mm});
            skLineSegment(sketch, "E743", {"start": v(-6.73, 10.5) * mm, "end": v(-6.23, 11.3) * mm});
            skLineSegment(sketch, "E744", {"start": v(-6.23, 11.3) * mm, "end": v(-5.67, 12.05) * mm});
            skLineSegment(sketch, "E745", {"start": v(-5.67, 12.05) * mm, "end": v(-4.39, 13.42) * mm});
            skLineSegment(sketch, "E746", {"start": v(-4.39, 13.42) * mm, "end": v(-2.9, 14.57) * mm});
            skLineSegment(sketch, "E747", {"start": v(-2.9, 14.57) * mm, "end": v(-1.92, 15.16) * mm});
            skLineSegment(sketch, "E748", {"start": v(-1.92, 15.16) * mm, "end": v(-0.9, 15.64) * mm});
            skLineSegment(sketch, "E749", {"start": v(-0.9, 15.64) * mm, "end": v(0.18, 16.01) * mm});
            skLineSegment(sketch, "E750", {"start": v(0.18, 16.01) * mm, "end": v(1.3, 16.27) * mm});
            skLineSegment(sketch, "E751", {"start": v(1.3, 16.27) * mm, "end": v(2.92, 16.4) * mm});
            skLineSegment(sketch, "E752", {"start": v(2.92, 16.4) * mm, "end": v(4.54, 16.23) * mm});
            skLineSegment(sketch, "E753", {"start": v(4.54, 16.23) * mm, "end": v(5.74, 15.92) * mm});
            skLineSegment(sketch, "E754", {"start": v(5.74, 15.92) * mm, "end": v(6.87, 15.46) * mm});
            skLineSegment(sketch, "E755", {"start": v(6.87, 15.46) * mm, "end": v(7.93, 14.86) * mm});
            skLineSegment(sketch, "E756", {"start": v(7.93, 14.86) * mm, "end": v(8.93, 14.13) * mm});
            skLineSegment(sketch, "E757", {"start": v(8.93, 14.13) * mm, "end": v(10.07, 13.05) * mm});
            skLineSegment(sketch, "E758", {"start": v(10.07, 13.05) * mm, "end": v(11.07, 11.85) * mm});
            skLineSegment(sketch, "E759", {"start": v(11.07, 11.85) * mm, "end": v(11.13, 11.73) * mm});
            skLineSegment(sketch, "E760", {"start": v(11.13, 11.73) * mm, "end": v(10.94, 11.75) * mm});
            skLineSegment(sketch, "E761", {"start": v(10.94, 11.75) * mm, "end": v(10.76, 11.8) * mm});
            skLineSegment(sketch, "E762", {"start": v(10.76, 11.8) * mm, "end": v(10.58, 11.87) * mm});
            skLineSegment(sketch, "E763", {"start": v(10.58, 11.87) * mm, "end": v(10.41, 11.93) * mm});
            skLineSegment(sketch, "E764", {"start": v(10.41, 11.93) * mm, "end": v(8.75, 12.37) * mm});
            skLineSegment(sketch, "E765", {"start": v(8.75, 12.37) * mm, "end": v(7.05, 12.7) * mm});
            skLineSegment(sketch, "E766", {"start": v(7.05, 12.7) * mm, "end": v(5.1, 12.84) * mm});
            skLineSegment(sketch, "E767", {"start": v(5.1, 12.84) * mm, "end": v(3.67, 12.75) * mm});
            skLineSegment(sketch, "E768", {"start": v(3.67, 12.75) * mm, "end": v(2.25, 12.48) * mm});
            skLineSegment(sketch, "E769", {"start": v(2.25, 12.48) * mm, "end": v(1.39, 12.2) * mm});
            skLineSegment(sketch, "E770", {"start": v(1.39, 12.2) * mm, "end": v(0.56, 11.86) * mm});
            skLineSegment(sketch, "E771", {"start": v(0.56, 11.86) * mm, "end": v(-0.23, 11.43) * mm});
            skLineSegment(sketch, "E772", {"start": v(-0.23, 11.43) * mm, "end": v(-0.97, 10.92) * mm});
            skLineSegment(sketch, "E773", {"start": v(-0.97, 10.92) * mm, "end": v(-2.16, 9.78) * mm});
            skLineSegment(sketch, "E774", {"start": v(-2.16, 9.78) * mm, "end": v(-3.12, 8.42) * mm});
            skLineSegment(sketch, "E775", {"start": v(-3.12, 8.42) * mm, "end": v(-3.86, 6.83) * mm});
            skLineSegment(sketch, "E776", {"start": v(-3.86, 6.83) * mm, "end": v(-4.33, 5.14) * mm});
            skLineSegment(sketch, "E777", {"start": v(-4.33, 5.14) * mm, "end": v(-4.47, 3.88) * mm});
            skLineSegment(sketch, "E778", {"start": v(-4.47, 3.88) * mm, "end": v(-4.48, 2.58) * mm});
            skLineSegment(sketch, "E779", {"start": v(-4.48, 2.58) * mm, "end": v(-4.34, 1.34) * mm});
            skLineSegment(sketch, "E780", {"start": v(-4.34, 1.34) * mm, "end": v(-4.06, 0.13) * mm});
            skLineSegment(sketch, "E781", {"start": v(-4.06, 0.13) * mm, "end": v(-3.5, -1.38) * mm});
            skLineSegment(sketch, "E782", {"start": v(-3.5, -1.38) * mm, "end": v(-2.67, -2.76) * mm});
            skLineSegment(sketch, "E783", {"start": v(-2.67, -2.76) * mm, "end": v(-2.32, -3.21) * mm});
            skLineSegment(sketch, "E784", {"start": v(-2.32, -3.21) * mm, "end": v(-1.95, -3.66) * mm});
            skLineSegment(sketch, "E785", {"start": v(-1.95, -3.66) * mm, "end": v(-1.93, -3.68) * mm});
            skLineSegment(sketch, "E786", {"start": v(-1.93, -3.68) * mm, "end": v(-1.9, -3.72) * mm});
            skLineSegment(sketch, "E787", {"start": v(-1.9, -3.72) * mm, "end": v(-1.9, -3.76) * mm});
            skLineSegment(sketch, "E788", {"start": v(-1.9, -3.76) * mm, "end": v(-1.93, -3.81) * mm});
            skSolve(sketch);
        }
        {
            var Q0;
            Q0 = qSketchRegion(id + "F9", true);
            extrude(context, id + "F10", {"entities" : qUnion([Q0]), "operationType" : NewBodyOperationType.ADD, "depth" : 1.5 * mm});
        }
        {
            var Q0;
            Q0=makeQuery(id+"F1.opExtrude","CAP_FACE",FACE,{"disambiguationData":[OSD([sQuery(id+"F0.wireOp",EDGE,"E0"),sQuery(id+"F0.wireOp",EDGE,"E1"),sQuery(id+"F0.wireOp",EDGE,"E2"),sQuery(id+"F0.wireOp",EDGE,"E3"),sQuery(id+"F0.wireOp",EDGE,"E4")])],"isStart":false});
            var sketch = newSketch(context, id + "F11", { "sketchPlane" : qUnion([Q0])});
            skLineSegment(sketch, "E789", {"start": v(-1.15, 9) * mm, "end": v(-0.77, 9.36) * mm});
            skLineSegment(sketch, "E790", {"start": v(-0.77, 9.36) * mm, "end": v(-0.35, 9.7) * mm});
            skLineSegment(sketch, "E791", {"start": v(-0.35, 9.7) * mm, "end": v(0.13, 10) * mm});
            skLineSegment(sketch, "E792", {"start": v(0.13, 10) * mm, "end": v(0.64, 10.28) * mm});
            skLineSegment(sketch, "E793", {"start": v(0.64, 10.28) * mm, "end": v(1.2, 10.52) * mm});
            skLineSegment(sketch, "E794", {"start": v(1.2, 10.52) * mm, "end": v(1.78, 10.73) * mm});
            skLineSegment(sketch, "E795", {"start": v(1.78, 10.73) * mm, "end": v(2.4, 10.89) * mm});
            skLineSegment(sketch, "E796", {"start": v(2.4, 10.89) * mm, "end": v(3.04, 11) * mm});
            skLineSegment(sketch, "E797", {"start": v(3.04, 11) * mm, "end": v(3.69, 11.07) * mm});
            skLineSegment(sketch, "E798", {"start": v(3.69, 11.07) * mm, "end": v(4.36, 11.08) * mm});
            skLineSegment(sketch, "E799", {"start": v(4.36, 11.08) * mm, "end": v(5.03, 11.03) * mm});
            skLineSegment(sketch, "E800", {"start": v(5.03, 11.03) * mm, "end": v(5.71, 10.92) * mm});
            skLineSegment(sketch, "E801", {"start": v(5.71, 10.92) * mm, "end": v(6.4, 10.75) * mm});
            skLineSegment(sketch, "E802", {"start": v(6.4, 10.75) * mm, "end": v(7.07, 10.51) * mm});
            skLineSegment(sketch, "E803", {"start": v(7.07, 10.51) * mm, "end": v(7.73, 10.2) * mm});
            skLineSegment(sketch, "E804", {"start": v(7.73, 10.2) * mm, "end": v(8.37, 9.81) * mm});
            skLineSegment(sketch, "E805", {"start": v(8.37, 9.81) * mm, "end": v(9, 9.35) * mm});
            skLineSegment(sketch, "E806", {"start": v(9, 9.35) * mm, "end": v(9.54, 8.83) * mm});
            skLineSegment(sketch, "E807", {"start": v(9.54, 8.83) * mm, "end": v(10.03, 8.27) * mm});
            skLineSegment(sketch, "E808", {"start": v(10.03, 8.27) * mm, "end": v(10.46, 7.67) * mm});
            skLineSegment(sketch, "E809", {"start": v(10.46, 7.67) * mm, "end": v(10.82, 7.03) * mm});
            skLineSegment(sketch, "E810", {"start": v(10.82, 7.03) * mm, "end": v(11.12, 6.36) * mm});
            skLineSegment(sketch, "E811", {"start": v(11.12, 6.36) * mm, "end": v(11.35, 5.68) * mm});
            skLineSegment(sketch, "E812", {"start": v(11.35, 5.68) * mm, "end": v(11.52, 4.98) * mm});
            skLineSegment(sketch, "E813", {"start": v(11.52, 4.98) * mm, "end": v(11.62, 4.27) * mm});
            skLineSegment(sketch, "E814", {"start": v(11.62, 4.27) * mm, "end": v(11.66, 3.55) * mm});
            skLineSegment(sketch, "E815", {"start": v(11.66, 3.55) * mm, "end": v(11.63, 2.85) * mm});
            skLineSegment(sketch, "E816", {"start": v(11.63, 2.85) * mm, "end": v(11.54, 2.15) * mm});
            skLineSegment(sketch, "E817", {"start": v(11.54, 2.15) * mm, "end": v(11.39, 1.47) * mm});
            skLineSegment(sketch, "E818", {"start": v(11.39, 1.47) * mm, "end": v(11.16, 0.8) * mm});
            skLineSegment(sketch, "E819", {"start": v(11.16, 0.8) * mm, "end": v(10.87, 0.18) * mm});
            skLineSegment(sketch, "E820", {"start": v(10.87, 0.18) * mm, "end": v(10.52, -0.41) * mm});
            skLineSegment(sketch, "E821", {"start": v(10.52, -0.41) * mm, "end": v(10.67, 0.32) * mm});
            skLineSegment(sketch, "E822", {"start": v(10.67, 0.32) * mm, "end": v(10.87, 1.56) * mm});
            skLineSegment(sketch, "E823", {"start": v(10.87, 1.56) * mm, "end": v(10.87, 2.82) * mm});
            skLineSegment(sketch, "E824", {"start": v(10.87, 2.82) * mm, "end": v(10.7, 4.05) * mm});
            skLineSegment(sketch, "E825", {"start": v(10.7, 4.05) * mm, "end": v(10.37, 5.22) * mm});
            skLineSegment(sketch, "E826", {"start": v(10.37, 5.22) * mm, "end": v(9.86, 6.32) * mm});
            skLineSegment(sketch, "E827", {"start": v(9.86, 6.32) * mm, "end": v(9.16, 7.34) * mm});
            skLineSegment(sketch, "E828", {"start": v(9.16, 7.34) * mm, "end": v(8.24, 8.3) * mm});
            skLineSegment(sketch, "E829", {"start": v(8.24, 8.3) * mm, "end": v(7.2, 9.06) * mm});
            skLineSegment(sketch, "E830", {"start": v(7.2, 9.06) * mm, "end": v(6.03, 9.63) * mm});
            skLineSegment(sketch, "E831", {"start": v(6.03, 9.63) * mm, "end": v(4.74, 9.99) * mm});
            skLineSegment(sketch, "E832", {"start": v(4.74, 9.99) * mm, "end": v(3.98, 10.11) * mm});
            skLineSegment(sketch, "E833", {"start": v(3.98, 10.11) * mm, "end": v(3.22, 10.15) * mm});
            skLineSegment(sketch, "E834", {"start": v(3.22, 10.15) * mm, "end": v(1.44, 9.94) * mm});
            skLineSegment(sketch, "E835", {"start": v(1.44, 9.94) * mm, "end": v(-0.27, 9.38) * mm});
            skLineSegment(sketch, "E836", {"start": v(-0.27, 9.38) * mm, "end": v(-0.69, 9.2) * mm});
            skLineSegment(sketch, "E837", {"start": v(-0.69, 9.2) * mm, "end": v(-1.15, 9) * mm});
            skSolve(sketch);
        }
        {
            var Q0;
            Q0 = qSketchRegion(id + "F11", true);
            extrude(context, id + "F12", {"entities" : qUnion([Q0]), "operationType" : NewBodyOperationType.ADD, "depth" : 2 * mm});
        }
        {
            var Q0;
            Q0=makeQuery(id+"F1.opExtrude","CAP_FACE",FACE,{"disambiguationData":[OSD([sQuery(id+"F0.wireOp",EDGE,"E0"),sQuery(id+"F0.wireOp",EDGE,"E1"),sQuery(id+"F0.wireOp",EDGE,"E2"),sQuery(id+"F0.wireOp",EDGE,"E3"),sQuery(id+"F0.wireOp",EDGE,"E4")])],"isStart":false});
            var sketch = newSketch(context, id + "F13", { "sketchPlane" : qUnion([Q0])});
            skLineSegment(sketch, "E838", {"start": v(1.2, -3.71) * mm, "end": v(1.32, -3.6) * mm});
            skLineSegment(sketch, "E839", {"start": v(1.32, -3.6) * mm, "end": v(1.46, -3.52) * mm});
            skLineSegment(sketch, "E840", {"start": v(1.46, -3.52) * mm, "end": v(1.6, -3.47) * mm});
            skLineSegment(sketch, "E841", {"start": v(1.6, -3.47) * mm, "end": v(1.72, -3.42) * mm});
            skLineSegment(sketch, "E842", {"start": v(1.72, -3.42) * mm, "end": v(3.23, -2.65) * mm});
            skLineSegment(sketch, "E843", {"start": v(3.23, -2.65) * mm, "end": v(4.62, -1.66) * mm});
            skLineSegment(sketch, "E844", {"start": v(4.62, -1.66) * mm, "end": v(5.3, -1) * mm});
            skLineSegment(sketch, "E845", {"start": v(5.3, -1) * mm, "end": v(5.88, -0.25) * mm});
            skLineSegment(sketch, "E846", {"start": v(5.88, -0.25) * mm, "end": v(6.33, 0.56) * mm});
            skLineSegment(sketch, "E847", {"start": v(6.33, 0.56) * mm, "end": v(6.65, 1.46) * mm});
            skLineSegment(sketch, "E848", {"start": v(6.65, 1.46) * mm, "end": v(6.8, 2.4) * mm});
            skLineSegment(sketch, "E849", {"start": v(6.8, 2.4) * mm, "end": v(6.8, 3.31) * mm});
            skLineSegment(sketch, "E850", {"start": v(6.8, 3.31) * mm, "end": v(6.62, 4.22) * mm});
            skLineSegment(sketch, "E851", {"start": v(6.62, 4.22) * mm, "end": v(6.3, 5.1) * mm});
            skLineSegment(sketch, "E852", {"start": v(6.3, 5.1) * mm, "end": v(5.96, 5.8) * mm});
            skLineSegment(sketch, "E853", {"start": v(5.96, 5.8) * mm, "end": v(5.54, 6.45) * mm});
            skLineSegment(sketch, "E854", {"start": v(5.54, 6.45) * mm, "end": v(5.05, 7.04) * mm});
            skLineSegment(sketch, "E855", {"start": v(5.05, 7.04) * mm, "end": v(4.5, 7.58) * mm});
            skLineSegment(sketch, "E856", {"start": v(4.5, 7.58) * mm, "end": v(3.84, 8.1) * mm});
            skLineSegment(sketch, "E857", {"start": v(3.84, 8.1) * mm, "end": v(3.14, 8.51) * mm});
            skLineSegment(sketch, "E858", {"start": v(3.14, 8.51) * mm, "end": v(2.38, 8.83) * mm});
            skLineSegment(sketch, "E859", {"start": v(2.38, 8.83) * mm, "end": v(1.57, 9.03) * mm});
            skLineSegment(sketch, "E860", {"start": v(1.57, 9.03) * mm, "end": v(1.36, 9.07) * mm});
            skLineSegment(sketch, "E861", {"start": v(1.36, 9.07) * mm, "end": v(1.1, 9.09) * mm});
            skLineSegment(sketch, "E862", {"start": v(1.1, 9.09) * mm, "end": v(1.26, 9.19) * mm});
            skLineSegment(sketch, "E863", {"start": v(1.26, 9.19) * mm, "end": v(1.41, 9.23) * mm});
            skLineSegment(sketch, "E864", {"start": v(1.41, 9.23) * mm, "end": v(1.56, 9.24) * mm});
            skLineSegment(sketch, "E865", {"start": v(1.56, 9.24) * mm, "end": v(1.68, 9.25) * mm});
            skLineSegment(sketch, "E866", {"start": v(1.68, 9.25) * mm, "end": v(2.8, 9.32) * mm});
            skLineSegment(sketch, "E867", {"start": v(2.8, 9.32) * mm, "end": v(3.9, 9.27) * mm});
            skLineSegment(sketch, "E868", {"start": v(3.9, 9.27) * mm, "end": v(4.98, 9.07) * mm});
            skLineSegment(sketch, "E869", {"start": v(4.98, 9.07) * mm, "end": v(6.03, 8.68) * mm});
            skLineSegment(sketch, "E870", {"start": v(6.03, 8.68) * mm, "end": v(6.83, 8.23) * mm});
            skLineSegment(sketch, "E871", {"start": v(6.83, 8.23) * mm, "end": v(7.52, 7.67) * mm});
            skLineSegment(sketch, "E872", {"start": v(7.52, 7.67) * mm, "end": v(8.12, 7) * mm});
            skLineSegment(sketch, "E873", {"start": v(8.12, 7) * mm, "end": v(8.62, 6.24) * mm});
            skLineSegment(sketch, "E874", {"start": v(8.62, 6.24) * mm, "end": v(9.06, 5.26) * mm});
            skLineSegment(sketch, "E875", {"start": v(9.06, 5.26) * mm, "end": v(9.33, 4.26) * mm});
            skLineSegment(sketch, "E876", {"start": v(9.33, 4.26) * mm, "end": v(9.46, 3.22) * mm});
            skLineSegment(sketch, "E877", {"start": v(9.46, 3.22) * mm, "end": v(9.43, 2.17) * mm});
            skLineSegment(sketch, "E878", {"start": v(9.43, 2.17) * mm, "end": v(9.2, 0.8) * mm});
            skLineSegment(sketch, "E879", {"start": v(9.2, 0.8) * mm, "end": v(8.74, -0.45) * mm});
            skLineSegment(sketch, "E880", {"start": v(8.74, -0.45) * mm, "end": v(8.04, -1.58) * mm});
            skLineSegment(sketch, "E881", {"start": v(8.04, -1.58) * mm, "end": v(7.09, -2.59) * mm});
            skLineSegment(sketch, "E882", {"start": v(7.09, -2.59) * mm, "end": v(6.42, -3.07) * mm});
            skLineSegment(sketch, "E883", {"start": v(6.42, -3.07) * mm, "end": v(5.7, -3.45) * mm});
            skLineSegment(sketch, "E884", {"start": v(5.7, -3.45) * mm, "end": v(4.94, -3.72) * mm});
            skLineSegment(sketch, "E885", {"start": v(4.94, -3.72) * mm, "end": v(4.13, -3.87) * mm});
            skLineSegment(sketch, "E886", {"start": v(4.13, -3.87) * mm, "end": v(2.67, -3.92) * mm});
            skLineSegment(sketch, "E887", {"start": v(2.67, -3.92) * mm, "end": v(1.2, -3.71) * mm});
            skSolve(sketch);
        }
        {
            var Q0;
            Q0 = qSketchRegion(id + "F13", true);
            extrude(context, id + "F14", {"entities" : qUnion([Q0]), "operationType" : NewBodyOperationType.ADD, "depth" : 2.5 * mm});
        }
    });
